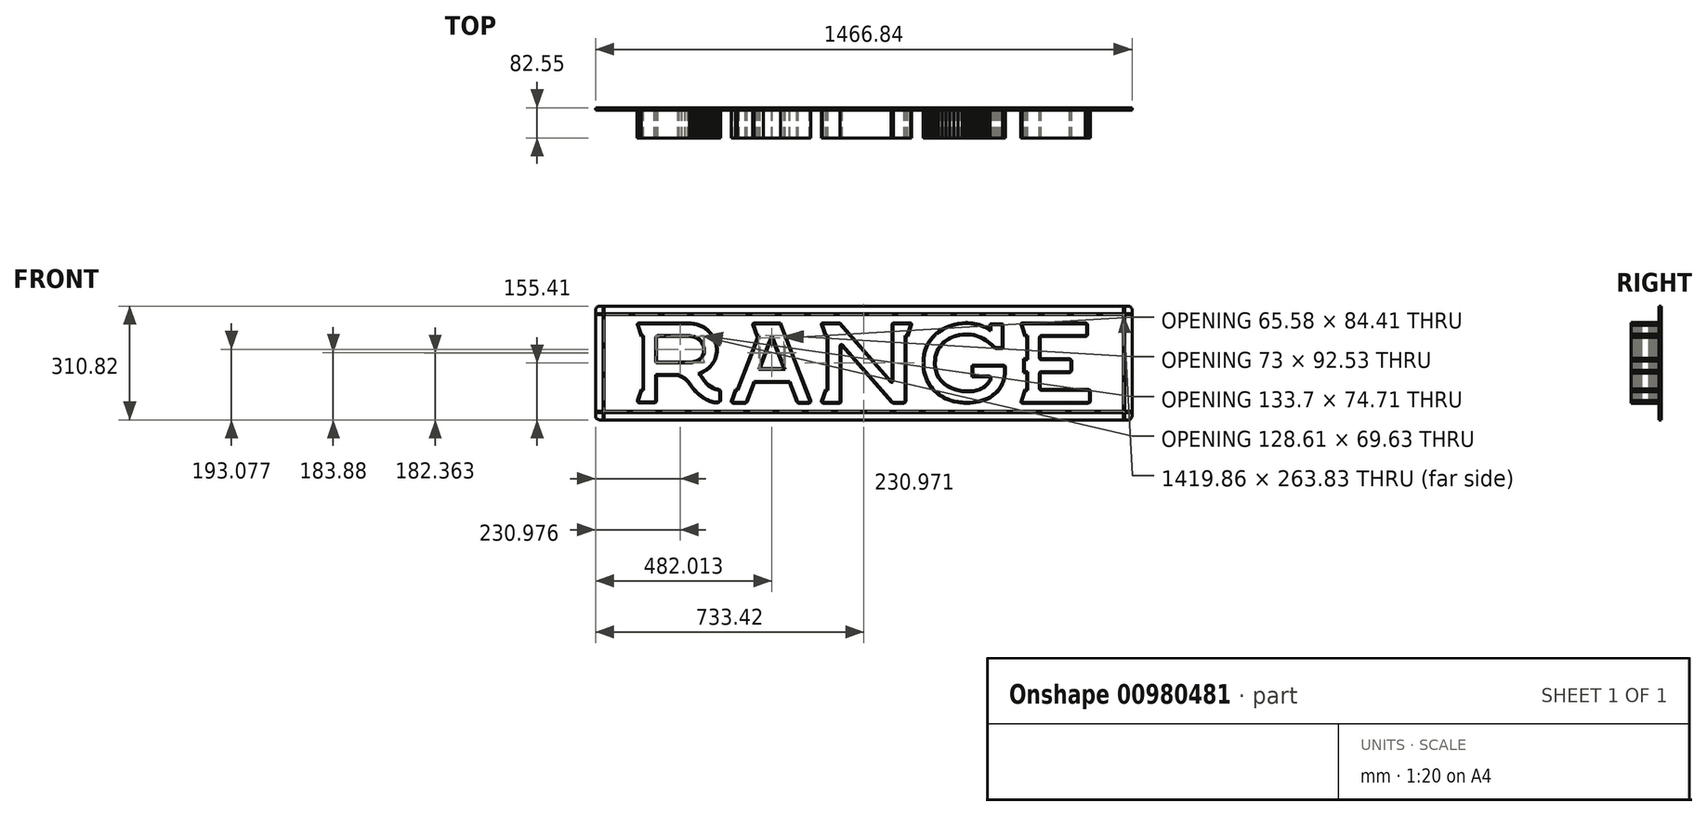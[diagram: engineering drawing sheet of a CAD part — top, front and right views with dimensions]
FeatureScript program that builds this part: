
annotation { "Feature Type Name" : "Feature", "Feature Type Description" : "" }
export const myFeature = defineFeature(function(context is Context, id is Id, definition is map)
    precondition{}
    {
        {
            var Q0;
            Q0=qCreatedBy(makeId("Front.planeOp"),FACE);
            var sketch = newSketch(context, id + "F0", { "sketchPlane" : qUnion([Q0])});
            skLineSegment(sketch, "E0", {"start": v(722.51, -155.4) * mm, "end": v(-722.52, -155.4) * mm});
            skLineSegment(sketch, "E1", {"start": v(-722.52, -155.4) * mm, "end": v(-723.06, -155.4) * mm});
            skLineSegment(sketch, "E2", {"start": v(-723.06, -155.4) * mm, "end": v(-724.71, -155.19) * mm});
            skLineSegment(sketch, "E3", {"start": v(-724.71, -155.19) * mm, "end": v(-726.76, -154.55) * mm});
            skLineSegment(sketch, "E4", {"start": v(-726.76, -154.55) * mm, "end": v(-728.62, -153.55) * mm});
            skLineSegment(sketch, "E5", {"start": v(-728.62, -153.55) * mm, "end": v(-730.23, -152.21) * mm});
            skLineSegment(sketch, "E6", {"start": v(-730.23, -152.21) * mm, "end": v(-731.56, -150.6) * mm});
            skLineSegment(sketch, "E7", {"start": v(-731.56, -150.6) * mm, "end": v(-732.57, -148.75) * mm});
            skLineSegment(sketch, "E8", {"start": v(-732.57, -148.75) * mm, "end": v(-733.2, -146.7) * mm});
            skLineSegment(sketch, "E9", {"start": v(-733.2, -146.7) * mm, "end": v(-733.43, -145.05) * mm});
            skLineSegment(sketch, "E10", {"start": v(-733.43, -145.05) * mm, "end": v(-733.43, -144.5) * mm});
            skLineSegment(sketch, "E11", {"start": v(-733.43, -144.5) * mm, "end": v(-733.43, 144.5) * mm});
            skLineSegment(sketch, "E12", {"start": v(-733.43, 144.5) * mm, "end": v(-733.43, 145.05) * mm});
            skLineSegment(sketch, "E13", {"start": v(-733.43, 145.05) * mm, "end": v(-733.2, 146.7) * mm});
            skLineSegment(sketch, "E14", {"start": v(-733.2, 146.7) * mm, "end": v(-732.57, 148.75) * mm});
            skLineSegment(sketch, "E15", {"start": v(-732.57, 148.75) * mm, "end": v(-731.56, 150.6) * mm});
            skLineSegment(sketch, "E16", {"start": v(-731.56, 150.6) * mm, "end": v(-730.23, 152.21) * mm});
            skLineSegment(sketch, "E17", {"start": v(-730.23, 152.21) * mm, "end": v(-728.62, 153.55) * mm});
            skLineSegment(sketch, "E18", {"start": v(-728.62, 153.55) * mm, "end": v(-726.76, 154.55) * mm});
            skLineSegment(sketch, "E19", {"start": v(-726.76, 154.55) * mm, "end": v(-724.71, 155.19) * mm});
            skLineSegment(sketch, "E20", {"start": v(-724.71, 155.19) * mm, "end": v(-723.06, 155.4) * mm});
            skLineSegment(sketch, "E21", {"start": v(-723.06, 155.4) * mm, "end": v(-722.52, 155.4) * mm});
            skLineSegment(sketch, "E22", {"start": v(-722.52, 155.4) * mm, "end": v(722.51, 155.4) * mm});
            skLineSegment(sketch, "E23", {"start": v(722.51, 155.4) * mm, "end": v(723.06, 155.4) * mm});
            skLineSegment(sketch, "E24", {"start": v(723.06, 155.4) * mm, "end": v(724.71, 155.19) * mm});
            skLineSegment(sketch, "E25", {"start": v(724.71, 155.19) * mm, "end": v(726.76, 154.55) * mm});
            skLineSegment(sketch, "E26", {"start": v(726.76, 154.55) * mm, "end": v(728.61, 153.55) * mm});
            skLineSegment(sketch, "E27", {"start": v(728.61, 153.55) * mm, "end": v(730.23, 152.21) * mm});
            skLineSegment(sketch, "E28", {"start": v(730.23, 152.21) * mm, "end": v(731.56, 150.6) * mm});
            skLineSegment(sketch, "E29", {"start": v(731.56, 150.6) * mm, "end": v(732.57, 148.75) * mm});
            skLineSegment(sketch, "E30", {"start": v(732.57, 148.75) * mm, "end": v(733.2, 146.7) * mm});
            skLineSegment(sketch, "E31", {"start": v(733.2, 146.7) * mm, "end": v(733.43, 145.05) * mm});
            skLineSegment(sketch, "E32", {"start": v(733.43, 145.05) * mm, "end": v(733.43, 144.5) * mm});
            skLineSegment(sketch, "E33", {"start": v(733.43, 144.5) * mm, "end": v(733.43, -144.5) * mm});
            skLineSegment(sketch, "E34", {"start": v(733.43, -144.5) * mm, "end": v(733.43, -145.05) * mm});
            skLineSegment(sketch, "E35", {"start": v(733.43, -145.05) * mm, "end": v(733.2, -146.7) * mm});
            skLineSegment(sketch, "E36", {"start": v(733.2, -146.7) * mm, "end": v(732.57, -148.75) * mm});
            skLineSegment(sketch, "E37", {"start": v(732.57, -148.75) * mm, "end": v(731.56, -150.6) * mm});
            skLineSegment(sketch, "E38", {"start": v(731.56, -150.6) * mm, "end": v(730.23, -152.21) * mm});
            skLineSegment(sketch, "E39", {"start": v(730.23, -152.21) * mm, "end": v(728.61, -153.55) * mm});
            skLineSegment(sketch, "E40", {"start": v(728.61, -153.55) * mm, "end": v(726.76, -154.55) * mm});
            skLineSegment(sketch, "E41", {"start": v(726.76, -154.55) * mm, "end": v(724.71, -155.19) * mm});
            skLineSegment(sketch, "E42", {"start": v(724.71, -155.19) * mm, "end": v(723.06, -155.4) * mm});
            skLineSegment(sketch, "E43", {"start": v(723.06, -155.4) * mm, "end": v(722.51, -155.4) * mm});
            skLineSegment(sketch, "E44", {"start": v(-733.43, 133.51) * mm, "end": v(733.43, 133.51) * mm});
            skLineSegment(sketch, "E45", {"start": v(-733.43, -133.51) * mm, "end": v(733.43, -133.51) * mm});
            skLineSegment(sketch, "E46", {"start": v(-711.53, 155.4) * mm, "end": v(-711.53, -155.4) * mm});
            skLineSegment(sketch, "E47", {"start": v(711.53, 155.4) * mm, "end": v(711.53, -155.4) * mm});
            skLineSegment(sketch, "E48", {"start": v(612.88, -107.15) * mm, "end": v(613.1, -107.15) * mm});
            skLineSegment(sketch, "E49", {"start": v(613.1, -107.15) * mm, "end": v(613.74, -107.06) * mm});
            skLineSegment(sketch, "E50", {"start": v(613.74, -107.06) * mm, "end": v(614.54, -106.82) * mm});
            skLineSegment(sketch, "E51", {"start": v(614.54, -106.82) * mm, "end": v(615.26, -106.42) * mm});
            skLineSegment(sketch, "E52", {"start": v(615.26, -106.42) * mm, "end": v(615.89, -105.9) * mm});
            skLineSegment(sketch, "E53", {"start": v(615.89, -105.9) * mm, "end": v(616.4, -105.27) * mm});
            skLineSegment(sketch, "E54", {"start": v(616.4, -105.27) * mm, "end": v(616.8, -104.55) * mm});
            skLineSegment(sketch, "E55", {"start": v(616.8, -104.55) * mm, "end": v(617.05, -103.75) * mm});
            skLineSegment(sketch, "E56", {"start": v(617.05, -103.75) * mm, "end": v(617.14, -103.1) * mm});
            skLineSegment(sketch, "E57", {"start": v(617.14, -103.1) * mm, "end": v(617.14, -102.9) * mm});
            skLineSegment(sketch, "E58", {"start": v(617.14, -102.9) * mm, "end": v(617.14, -79.01) * mm});
            skLineSegment(sketch, "E59", {"start": v(617.14, -79.01) * mm, "end": v(617.14, -78.8) * mm});
            skLineSegment(sketch, "E60", {"start": v(617.14, -78.8) * mm, "end": v(617.05, -78.15) * mm});
            skLineSegment(sketch, "E61", {"start": v(617.05, -78.15) * mm, "end": v(616.8, -77.35) * mm});
            skLineSegment(sketch, "E62", {"start": v(616.8, -77.35) * mm, "end": v(616.4, -76.63) * mm});
            skLineSegment(sketch, "E63", {"start": v(616.4, -76.63) * mm, "end": v(615.89, -76) * mm});
            skLineSegment(sketch, "E64", {"start": v(615.89, -76) * mm, "end": v(615.26, -75.48) * mm});
            skLineSegment(sketch, "E65", {"start": v(615.26, -75.48) * mm, "end": v(614.54, -75.09) * mm});
            skLineSegment(sketch, "E66", {"start": v(614.54, -75.09) * mm, "end": v(613.74, -74.84) * mm});
            skLineSegment(sketch, "E67", {"start": v(613.74, -74.84) * mm, "end": v(613.1, -74.75) * mm});
            skLineSegment(sketch, "E68", {"start": v(613.1, -74.75) * mm, "end": v(612.88, -74.75) * mm});
            skLineSegment(sketch, "E69", {"start": v(612.88, -74.75) * mm, "end": v(484.52, -74.75) * mm});
            skLineSegment(sketch, "E70", {"start": v(484.52, -74.75) * mm, "end": v(484.3, -74.75) * mm});
            skLineSegment(sketch, "E71", {"start": v(484.3, -74.75) * mm, "end": v(483.65, -74.67) * mm});
            skLineSegment(sketch, "E72", {"start": v(483.65, -74.67) * mm, "end": v(482.85, -74.42) * mm});
            skLineSegment(sketch, "E73", {"start": v(482.85, -74.42) * mm, "end": v(482.12, -74.02) * mm});
            skLineSegment(sketch, "E74", {"start": v(482.12, -74.02) * mm, "end": v(481.48, -73.5) * mm});
            skLineSegment(sketch, "E75", {"start": v(481.48, -73.5) * mm, "end": v(480.96, -72.86) * mm});
            skLineSegment(sketch, "E76", {"start": v(480.96, -72.86) * mm, "end": v(480.57, -72.13) * mm});
            skLineSegment(sketch, "E77", {"start": v(480.57, -72.13) * mm, "end": v(480.31, -71.33) * mm});
            skLineSegment(sketch, "E78", {"start": v(480.31, -71.33) * mm, "end": v(480.23, -70.68) * mm});
            skLineSegment(sketch, "E79", {"start": v(480.23, -70.68) * mm, "end": v(480.23, -70.46) * mm});
            skLineSegment(sketch, "E80", {"start": v(480.23, -70.46) * mm, "end": v(480.23, -27.81) * mm});
            skLineSegment(sketch, "E81", {"start": v(480.23, -27.81) * mm, "end": v(480.23, -27.6) * mm});
            skLineSegment(sketch, "E82", {"start": v(480.23, -27.6) * mm, "end": v(480.31, -26.95) * mm});
            skLineSegment(sketch, "E83", {"start": v(480.31, -26.95) * mm, "end": v(480.57, -26.14) * mm});
            skLineSegment(sketch, "E84", {"start": v(480.57, -26.14) * mm, "end": v(480.96, -25.41) * mm});
            skLineSegment(sketch, "E85", {"start": v(480.96, -25.41) * mm, "end": v(481.48, -24.78) * mm});
            skLineSegment(sketch, "E86", {"start": v(481.48, -24.78) * mm, "end": v(482.12, -24.25) * mm});
            skLineSegment(sketch, "E87", {"start": v(482.12, -24.25) * mm, "end": v(482.85, -23.86) * mm});
            skLineSegment(sketch, "E88", {"start": v(482.85, -23.86) * mm, "end": v(483.65, -23.6) * mm});
            skLineSegment(sketch, "E89", {"start": v(483.65, -23.6) * mm, "end": v(484.3, -23.52) * mm});
            skLineSegment(sketch, "E90", {"start": v(484.3, -23.52) * mm, "end": v(484.52, -23.52) * mm});
            skLineSegment(sketch, "E91", {"start": v(484.52, -23.52) * mm, "end": v(561.84, -23.52) * mm});
            skLineSegment(sketch, "E92", {"start": v(561.84, -23.52) * mm, "end": v(562.05, -23.52) * mm});
            skLineSegment(sketch, "E93", {"start": v(562.05, -23.52) * mm, "end": v(562.7, -23.44) * mm});
            skLineSegment(sketch, "E94", {"start": v(562.7, -23.44) * mm, "end": v(563.5, -23.19) * mm});
            skLineSegment(sketch, "E95", {"start": v(563.5, -23.19) * mm, "end": v(564.22, -22.8) * mm});
            skLineSegment(sketch, "E96", {"start": v(564.22, -22.8) * mm, "end": v(564.85, -22.27) * mm});
            skLineSegment(sketch, "E97", {"start": v(564.85, -22.27) * mm, "end": v(565.37, -21.64) * mm});
            skLineSegment(sketch, "E98", {"start": v(565.37, -21.64) * mm, "end": v(565.76, -20.92) * mm});
            skLineSegment(sketch, "E99", {"start": v(565.76, -20.92) * mm, "end": v(566.01, -20.12) * mm});
            skLineSegment(sketch, "E100", {"start": v(566.01, -20.12) * mm, "end": v(566.1, -19.48) * mm});
            skLineSegment(sketch, "E101", {"start": v(566.1, -19.48) * mm, "end": v(566.1, -19.26) * mm});
            skLineSegment(sketch, "E102", {"start": v(566.1, -19.26) * mm, "end": v(566.1, 4.62) * mm});
            skLineSegment(sketch, "E103", {"start": v(566.1, 4.62) * mm, "end": v(566.1, 4.83) * mm});
            skLineSegment(sketch, "E104", {"start": v(566.1, 4.83) * mm, "end": v(566.01, 5.48) * mm});
            skLineSegment(sketch, "E105", {"start": v(566.01, 5.48) * mm, "end": v(565.76, 6.28) * mm});
            skLineSegment(sketch, "E106", {"start": v(565.76, 6.28) * mm, "end": v(565.37, 7) * mm});
            skLineSegment(sketch, "E107", {"start": v(565.37, 7) * mm, "end": v(564.85, 7.63) * mm});
            skLineSegment(sketch, "E108", {"start": v(564.85, 7.63) * mm, "end": v(564.22, 8.15) * mm});
            skLineSegment(sketch, "E109", {"start": v(564.22, 8.15) * mm, "end": v(563.5, 8.54) * mm});
            skLineSegment(sketch, "E110", {"start": v(563.5, 8.54) * mm, "end": v(562.7, 8.8) * mm});
            skLineSegment(sketch, "E111", {"start": v(562.7, 8.8) * mm, "end": v(562.05, 8.88) * mm});
            skLineSegment(sketch, "E112", {"start": v(562.05, 8.88) * mm, "end": v(561.84, 8.88) * mm});
            skLineSegment(sketch, "E113", {"start": v(561.84, 8.88) * mm, "end": v(484.52, 8.88) * mm});
            skLineSegment(sketch, "E114", {"start": v(484.52, 8.88) * mm, "end": v(484.3, 8.88) * mm});
            skLineSegment(sketch, "E115", {"start": v(484.3, 8.88) * mm, "end": v(483.65, 8.96) * mm});
            skLineSegment(sketch, "E116", {"start": v(483.65, 8.96) * mm, "end": v(482.85, 9.21) * mm});
            skLineSegment(sketch, "E117", {"start": v(482.85, 9.21) * mm, "end": v(482.12, 9.6) * mm});
            skLineSegment(sketch, "E118", {"start": v(482.12, 9.6) * mm, "end": v(481.48, 10.13) * mm});
            skLineSegment(sketch, "E119", {"start": v(481.48, 10.13) * mm, "end": v(480.96, 10.77) * mm});
            skLineSegment(sketch, "E120", {"start": v(480.96, 10.77) * mm, "end": v(480.57, 11.5) * mm});
            skLineSegment(sketch, "E121", {"start": v(480.57, 11.5) * mm, "end": v(480.31, 12.3) * mm});
            skLineSegment(sketch, "E122", {"start": v(480.31, 12.3) * mm, "end": v(480.23, 12.95) * mm});
            skLineSegment(sketch, "E123", {"start": v(480.23, 12.95) * mm, "end": v(480.23, 13.17) * mm});
            skLineSegment(sketch, "E124", {"start": v(480.23, 13.17) * mm, "end": v(480.23, 70.45) * mm});
            skLineSegment(sketch, "E125", {"start": v(480.23, 70.45) * mm, "end": v(480.23, 70.66) * mm});
            skLineSegment(sketch, "E126", {"start": v(480.23, 70.66) * mm, "end": v(480.31, 71.31) * mm});
            skLineSegment(sketch, "E127", {"start": v(480.31, 71.31) * mm, "end": v(480.57, 72.12) * mm});
            skLineSegment(sketch, "E128", {"start": v(480.57, 72.12) * mm, "end": v(480.96, 72.85) * mm});
            skLineSegment(sketch, "E129", {"start": v(480.96, 72.85) * mm, "end": v(481.48, 73.48) * mm});
            skLineSegment(sketch, "E130", {"start": v(481.48, 73.48) * mm, "end": v(482.12, 74) * mm});
            skLineSegment(sketch, "E131", {"start": v(482.12, 74) * mm, "end": v(482.85, 74.4) * mm});
            skLineSegment(sketch, "E132", {"start": v(482.85, 74.4) * mm, "end": v(483.65, 74.65) * mm});
            skLineSegment(sketch, "E133", {"start": v(483.65, 74.65) * mm, "end": v(484.3, 74.74) * mm});
            skLineSegment(sketch, "E134", {"start": v(484.3, 74.74) * mm, "end": v(484.52, 74.74) * mm});
            skLineSegment(sketch, "E135", {"start": v(484.52, 74.74) * mm, "end": v(605.39, 74.74) * mm});
            skLineSegment(sketch, "E136", {"start": v(605.39, 74.74) * mm, "end": v(605.6, 74.74) * mm});
            skLineSegment(sketch, "E137", {"start": v(605.6, 74.74) * mm, "end": v(606.24, 74.82) * mm});
            skLineSegment(sketch, "E138", {"start": v(606.24, 74.82) * mm, "end": v(607.04, 75.07) * mm});
            skLineSegment(sketch, "E139", {"start": v(607.04, 75.07) * mm, "end": v(607.77, 75.46) * mm});
            skLineSegment(sketch, "E140", {"start": v(607.77, 75.46) * mm, "end": v(608.4, 75.98) * mm});
            skLineSegment(sketch, "E141", {"start": v(608.4, 75.98) * mm, "end": v(608.92, 76.61) * mm});
            skLineSegment(sketch, "E142", {"start": v(608.92, 76.61) * mm, "end": v(609.31, 77.34) * mm});
            skLineSegment(sketch, "E143", {"start": v(609.31, 77.34) * mm, "end": v(609.56, 78.14) * mm});
            skLineSegment(sketch, "E144", {"start": v(609.56, 78.14) * mm, "end": v(609.65, 78.78) * mm});
            skLineSegment(sketch, "E145", {"start": v(609.65, 78.78) * mm, "end": v(609.65, 79) * mm});
            skLineSegment(sketch, "E146", {"start": v(609.65, 79) * mm, "end": v(609.65, 102.87) * mm});
            skLineSegment(sketch, "E147", {"start": v(609.65, 102.87) * mm, "end": v(609.65, 103.08) * mm});
            skLineSegment(sketch, "E148", {"start": v(609.65, 103.08) * mm, "end": v(609.56, 103.73) * mm});
            skLineSegment(sketch, "E149", {"start": v(609.56, 103.73) * mm, "end": v(609.31, 104.53) * mm});
            skLineSegment(sketch, "E150", {"start": v(609.31, 104.53) * mm, "end": v(608.92, 105.25) * mm});
            skLineSegment(sketch, "E151", {"start": v(608.92, 105.25) * mm, "end": v(608.4, 105.88) * mm});
            skLineSegment(sketch, "E152", {"start": v(608.4, 105.88) * mm, "end": v(607.77, 106.4) * mm});
            skLineSegment(sketch, "E153", {"start": v(607.77, 106.4) * mm, "end": v(607.04, 106.8) * mm});
            skLineSegment(sketch, "E154", {"start": v(607.04, 106.8) * mm, "end": v(606.24, 107.04) * mm});
            skLineSegment(sketch, "E155", {"start": v(606.24, 107.04) * mm, "end": v(605.6, 107.13) * mm});
            skLineSegment(sketch, "E156", {"start": v(605.6, 107.13) * mm, "end": v(605.39, 107.13) * mm});
            skLineSegment(sketch, "E157", {"start": v(605.39, 107.13) * mm, "end": v(433.74, 107.13) * mm});
            skLineSegment(sketch, "E158", {"start": v(433.74, 107.13) * mm, "end": v(433.54, 107.13) * mm});
            skLineSegment(sketch, "E159", {"start": v(433.54, 107.13) * mm, "end": v(432.94, 106.94) * mm});
            skLineSegment(sketch, "E160", {"start": v(432.94, 106.94) * mm, "end": v(432.4, 106.51) * mm});
            skLineSegment(sketch, "E161", {"start": v(432.4, 106.51) * mm, "end": v(432.31, 106.4) * mm});
            skLineSegment(sketch, "E162", {"start": v(432.31, 106.4) * mm, "end": v(432.23, 106.28) * mm});
            skLineSegment(sketch, "E163", {"start": v(432.23, 106.28) * mm, "end": v(432, 105.64) * mm});
            skLineSegment(sketch, "E164", {"start": v(432, 105.64) * mm, "end": v(432.03, 104.95) * mm});
            skLineSegment(sketch, "E165", {"start": v(432.03, 104.95) * mm, "end": v(432.07, 104.81) * mm});
            skLineSegment(sketch, "E166", {"start": v(432.07, 104.81) * mm, "end": v(442.1, 74.74) * mm});
            skLineSegment(sketch, "E167", {"start": v(442.1, 74.74) * mm, "end": v(447.83, 74.74) * mm});
            skLineSegment(sketch, "E168", {"start": v(447.83, 74.74) * mm, "end": v(447.83, 8.88) * mm});
            skLineSegment(sketch, "E169", {"start": v(447.83, 8.88) * mm, "end": v(438.64, 8.88) * mm});
            skLineSegment(sketch, "E170", {"start": v(438.64, 8.88) * mm, "end": v(438.64, -23.52) * mm});
            skLineSegment(sketch, "E171", {"start": v(438.64, -23.52) * mm, "end": v(447.83, -23.52) * mm});
            skLineSegment(sketch, "E172", {"start": v(447.83, -23.52) * mm, "end": v(447.83, -74.75) * mm});
            skLineSegment(sketch, "E173", {"start": v(447.83, -74.75) * mm, "end": v(442.1, -74.75) * mm});
            skLineSegment(sketch, "E174", {"start": v(442.1, -74.75) * mm, "end": v(432, -105.07) * mm});
            skLineSegment(sketch, "E175", {"start": v(432, -105.07) * mm, "end": v(431.95, -105.19) * mm});
            skLineSegment(sketch, "E176", {"start": v(431.95, -105.19) * mm, "end": v(431.93, -105.8) * mm});
            skLineSegment(sketch, "E177", {"start": v(431.93, -105.8) * mm, "end": v(432.14, -106.39) * mm});
            skLineSegment(sketch, "E178", {"start": v(432.14, -106.39) * mm, "end": v(432.2, -106.5) * mm});
            skLineSegment(sketch, "E179", {"start": v(432.2, -106.5) * mm, "end": v(432.28, -106.6) * mm});
            skLineSegment(sketch, "E180", {"start": v(432.28, -106.6) * mm, "end": v(432.77, -106.98) * mm});
            skLineSegment(sketch, "E181", {"start": v(432.77, -106.98) * mm, "end": v(433.31, -107.15) * mm});
            skLineSegment(sketch, "E182", {"start": v(433.31, -107.15) * mm, "end": v(433.5, -107.15) * mm});
            skLineSegment(sketch, "E183", {"start": v(433.5, -107.15) * mm, "end": v(612.88, -107.15) * mm});
            skLineSegment(sketch, "E184", {"start": v(-569.3, 6.46) * mm, "end": v(-569.3, 68.88) * mm});
            skLineSegment(sketch, "E185", {"start": v(-569.3, 68.88) * mm, "end": v(-569.3, 69.47) * mm});
            skLineSegment(sketch, "E186", {"start": v(-569.3, 69.47) * mm, "end": v(-568.81, 71.27) * mm});
            skLineSegment(sketch, "E187", {"start": v(-568.81, 71.27) * mm, "end": v(-567.49, 73.22) * mm});
            skLineSegment(sketch, "E188", {"start": v(-567.49, 73.22) * mm, "end": v(-565.53, 74.54) * mm});
            skLineSegment(sketch, "E189", {"start": v(-565.53, 74.54) * mm, "end": v(-563.74, 75.02) * mm});
            skLineSegment(sketch, "E190", {"start": v(-563.74, 75.02) * mm, "end": v(-563.14, 75.02) * mm});
            skLineSegment(sketch, "E191", {"start": v(-563.14, 75.02) * mm, "end": v(-477.07, 75.02) * mm});
            skLineSegment(sketch, "E192", {"start": v(-477.07, 75.02) * mm, "end": v(-475.23, 75.02) * mm});
            skLineSegment(sketch, "E193", {"start": v(-475.23, 75.02) * mm, "end": v(-469.7, 74.4) * mm});
            skLineSegment(sketch, "E194", {"start": v(-469.7, 74.4) * mm, "end": v(-462.75, 72.63) * mm});
            skLineSegment(sketch, "E195", {"start": v(-462.75, 72.63) * mm, "end": v(-456.31, 69.79) * mm});
            skLineSegment(sketch, "E196", {"start": v(-456.31, 69.79) * mm, "end": v(-450.52, 65.98) * mm});
            skLineSegment(sketch, "E197", {"start": v(-450.52, 65.98) * mm, "end": v(-445.51, 61.3) * mm});
            skLineSegment(sketch, "E198", {"start": v(-445.51, 61.3) * mm, "end": v(-441.4, 55.84) * mm});
            skLineSegment(sketch, "E199", {"start": v(-441.4, 55.84) * mm, "end": v(-438.3, 49.72) * mm});
            skLineSegment(sketch, "E200", {"start": v(-438.3, 49.72) * mm, "end": v(-436.68, 44.72) * mm});
            skLineSegment(sketch, "E201", {"start": v(-436.68, 44.72) * mm, "end": v(-436.35, 43.02) * mm});
            skLineSegment(sketch, "E202", {"start": v(-436.35, 43.02) * mm, "end": v(-435.97, 41.04) * mm});
            skLineSegment(sketch, "E203", {"start": v(-435.97, 41.04) * mm, "end": v(-435.6, 34.97) * mm});
            skLineSegment(sketch, "E204", {"start": v(-435.6, 34.97) * mm, "end": v(-436.48, 27.4) * mm});
            skLineSegment(sketch, "E205", {"start": v(-436.48, 27.4) * mm, "end": v(-438.97, 20.44) * mm});
            skLineSegment(sketch, "E206", {"start": v(-438.97, 20.44) * mm, "end": v(-441.87, 15.6) * mm});
            skLineSegment(sketch, "E207", {"start": v(-441.87, 15.6) * mm, "end": v(-443.05, 14.17) * mm});
            skLineSegment(sketch, "E208", {"start": v(-443.05, 14.17) * mm, "end": v(-443.73, 13.34) * mm});
            skLineSegment(sketch, "E209", {"start": v(-443.73, 13.34) * mm, "end": v(-446, 11.04) * mm});
            skLineSegment(sketch, "E210", {"start": v(-446, 11.04) * mm, "end": v(-449.32, 8.29) * mm});
            skLineSegment(sketch, "E211", {"start": v(-449.32, 8.29) * mm, "end": v(-453, 5.91) * mm});
            skLineSegment(sketch, "E212", {"start": v(-453, 5.91) * mm, "end": v(-456.99, 3.94) * mm});
            skLineSegment(sketch, "E213", {"start": v(-456.99, 3.94) * mm, "end": v(-461.26, 2.37) * mm});
            skLineSegment(sketch, "E214", {"start": v(-461.26, 2.37) * mm, "end": v(-465.79, 1.24) * mm});
            skLineSegment(sketch, "E215", {"start": v(-465.79, 1.24) * mm, "end": v(-470.52, 0.54) * mm});
            skLineSegment(sketch, "E216", {"start": v(-470.52, 0.54) * mm, "end": v(-474.2, 0.31) * mm});
            skLineSegment(sketch, "E217", {"start": v(-474.2, 0.31) * mm, "end": v(-475.42, 0.31) * mm});
            skLineSegment(sketch, "E218", {"start": v(-475.42, 0.31) * mm, "end": v(-563.14, 0.31) * mm});
            skLineSegment(sketch, "E219", {"start": v(-563.14, 0.31) * mm, "end": v(-563.74, 0.31) * mm});
            skLineSegment(sketch, "E220", {"start": v(-563.74, 0.31) * mm, "end": v(-565.53, 0.8) * mm});
            skLineSegment(sketch, "E221", {"start": v(-565.53, 0.8) * mm, "end": v(-567.49, 2.11) * mm});
            skLineSegment(sketch, "E222", {"start": v(-567.49, 2.11) * mm, "end": v(-568.81, 4.07) * mm});
            skLineSegment(sketch, "E223", {"start": v(-568.81, 4.07) * mm, "end": v(-569.3, 5.86) * mm});
            skLineSegment(sketch, "E224", {"start": v(-569.3, 5.86) * mm, "end": v(-569.3, 6.46) * mm});
            skLineSegment(sketch, "E225", {"start": v(-472.9, -59.01) * mm, "end": v(-471.86, -60.6) * mm});
            skLineSegment(sketch, "E226", {"start": v(-471.86, -60.6) * mm, "end": v(-468.53, -65.25) * mm});
            skLineSegment(sketch, "E227", {"start": v(-468.53, -65.25) * mm, "end": v(-463.99, -71) * mm});
            skLineSegment(sketch, "E228", {"start": v(-463.99, -71) * mm, "end": v(-459.31, -76.26) * mm});
            skLineSegment(sketch, "E229", {"start": v(-459.31, -76.26) * mm, "end": v(-454.54, -81.06) * mm});
            skLineSegment(sketch, "E230", {"start": v(-454.54, -81.06) * mm, "end": v(-449.7, -85.4) * mm});
            skLineSegment(sketch, "E231", {"start": v(-449.7, -85.4) * mm, "end": v(-444.84, -89.3) * mm});
            skLineSegment(sketch, "E232", {"start": v(-444.84, -89.3) * mm, "end": v(-439.99, -92.77) * mm});
            skLineSegment(sketch, "E233", {"start": v(-439.99, -92.77) * mm, "end": v(-435.19, -95.82) * mm});
            skLineSegment(sketch, "E234", {"start": v(-435.19, -95.82) * mm, "end": v(-430.47, -98.47) * mm});
            skLineSegment(sketch, "E235", {"start": v(-430.47, -98.47) * mm, "end": v(-425.87, -100.73) * mm});
            skLineSegment(sketch, "E236", {"start": v(-425.87, -100.73) * mm, "end": v(-421.43, -102.62) * mm});
            skLineSegment(sketch, "E237", {"start": v(-421.43, -102.62) * mm, "end": v(-417.18, -104.14) * mm});
            skLineSegment(sketch, "E238", {"start": v(-417.18, -104.14) * mm, "end": v(-413.16, -105.31) * mm});
            skLineSegment(sketch, "E239", {"start": v(-413.16, -105.31) * mm, "end": v(-409.4, -106.15) * mm});
            skLineSegment(sketch, "E240", {"start": v(-409.4, -106.15) * mm, "end": v(-405.95, -106.66) * mm});
            skLineSegment(sketch, "E241", {"start": v(-405.95, -106.66) * mm, "end": v(-403.61, -106.85) * mm});
            skLineSegment(sketch, "E242", {"start": v(-403.61, -106.85) * mm, "end": v(-402.84, -106.86) * mm});
            skLineSegment(sketch, "E243", {"start": v(-402.84, -106.86) * mm, "end": v(-402.13, -106.86) * mm});
            skLineSegment(sketch, "E244", {"start": v(-402.13, -106.86) * mm, "end": v(-398.9, -106.23) * mm});
            skLineSegment(sketch, "E245", {"start": v(-398.9, -106.23) * mm, "end": v(-396.26, -104.76) * mm});
            skLineSegment(sketch, "E246", {"start": v(-396.26, -104.76) * mm, "end": v(-395.84, -104.36) * mm});
            skLineSegment(sketch, "E247", {"start": v(-395.84, -104.36) * mm, "end": v(-395.6, -104.12) * mm});
            skLineSegment(sketch, "E248", {"start": v(-395.6, -104.12) * mm, "end": v(-394.97, -103.3) * mm});
            skLineSegment(sketch, "E249", {"start": v(-394.97, -103.3) * mm, "end": v(-394.34, -102.12) * mm});
            skLineSegment(sketch, "E250", {"start": v(-394.34, -102.12) * mm, "end": v(-393.95, -100.82) * mm});
            skLineSegment(sketch, "E251", {"start": v(-393.95, -100.82) * mm, "end": v(-393.82, -99.77) * mm});
            skLineSegment(sketch, "E252", {"start": v(-393.82, -99.77) * mm, "end": v(-393.82, -99.42) * mm});
            skLineSegment(sketch, "E253", {"start": v(-393.82, -99.42) * mm, "end": v(-393.85, -80.15) * mm});
            skLineSegment(sketch, "E254", {"start": v(-393.85, -80.15) * mm, "end": v(-393.85, -79.63) * mm});
            skLineSegment(sketch, "E255", {"start": v(-393.85, -79.63) * mm, "end": v(-394.21, -78.07) * mm});
            skLineSegment(sketch, "E256", {"start": v(-394.21, -78.07) * mm, "end": v(-395.21, -76.3) * mm});
            skLineSegment(sketch, "E257", {"start": v(-395.21, -76.3) * mm, "end": v(-396.73, -74.96) * mm});
            skLineSegment(sketch, "E258", {"start": v(-396.73, -74.96) * mm, "end": v(-398.16, -74.3) * mm});
            skLineSegment(sketch, "E259", {"start": v(-398.16, -74.3) * mm, "end": v(-398.65, -74.2) * mm});
            skLineSegment(sketch, "E260", {"start": v(-398.65, -74.2) * mm, "end": v(-399.75, -73.99) * mm});
            skLineSegment(sketch, "E261", {"start": v(-399.75, -73.99) * mm, "end": v(-403.01, -73.18) * mm});
            skLineSegment(sketch, "E262", {"start": v(-403.01, -73.18) * mm, "end": v(-408.05, -71.55) * mm});
            skLineSegment(sketch, "E263", {"start": v(-408.05, -71.55) * mm, "end": v(-413.6, -69.2) * mm});
            skLineSegment(sketch, "E264", {"start": v(-413.6, -69.2) * mm, "end": v(-419.45, -65.98) * mm});
            skLineSegment(sketch, "E265", {"start": v(-419.45, -65.98) * mm, "end": v(-425.46, -61.77) * mm});
            skLineSegment(sketch, "E266", {"start": v(-425.46, -61.77) * mm, "end": v(-431.42, -56.42) * mm});
            skLineSegment(sketch, "E267", {"start": v(-431.42, -56.42) * mm, "end": v(-437.17, -49.8) * mm});
            skLineSegment(sketch, "E268", {"start": v(-437.17, -49.8) * mm, "end": v(-441.31, -43.86) * mm});
            skLineSegment(sketch, "E269", {"start": v(-441.31, -43.86) * mm, "end": v(-442.52, -41.78) * mm});
            skLineSegment(sketch, "E270", {"start": v(-442.52, -41.78) * mm, "end": v(-443.1, -40.78) * mm});
            skLineSegment(sketch, "E271", {"start": v(-443.1, -40.78) * mm, "end": v(-446.55, -35.78) * mm});
            skLineSegment(sketch, "E272", {"start": v(-446.55, -35.78) * mm, "end": v(-450.7, -30.84) * mm});
            skLineSegment(sketch, "E273", {"start": v(-450.7, -30.84) * mm, "end": v(-451.62, -29.86) * mm});
            skLineSegment(sketch, "E274", {"start": v(-451.62, -29.86) * mm, "end": v(-452.97, -28.45) * mm});
            skLineSegment(sketch, "E275", {"start": v(-452.97, -28.45) * mm, "end": v(-451.12, -27.8) * mm});
            skLineSegment(sketch, "E276", {"start": v(-451.12, -27.8) * mm, "end": v(-449.62, -27.27) * mm});
            skLineSegment(sketch, "E277", {"start": v(-449.62, -27.27) * mm, "end": v(-445.2, -25.47) * mm});
            skLineSegment(sketch, "E278", {"start": v(-445.2, -25.47) * mm, "end": v(-439.6, -22.8) * mm});
            skLineSegment(sketch, "E279", {"start": v(-439.6, -22.8) * mm, "end": v(-434.38, -19.78) * mm});
            skLineSegment(sketch, "E280", {"start": v(-434.38, -19.78) * mm, "end": v(-429.52, -16.45) * mm});
            skLineSegment(sketch, "E281", {"start": v(-429.52, -16.45) * mm, "end": v(-425.03, -12.82) * mm});
            skLineSegment(sketch, "E282", {"start": v(-425.03, -12.82) * mm, "end": v(-420.93, -8.9) * mm});
            skLineSegment(sketch, "E283", {"start": v(-420.93, -8.9) * mm, "end": v(-417.24, -4.7) * mm});
            skLineSegment(sketch, "E284", {"start": v(-417.24, -4.7) * mm, "end": v(-413.95, -0.26) * mm});
            skLineSegment(sketch, "E285", {"start": v(-413.95, -0.26) * mm, "end": v(-411.07, 4.43) * mm});
            skLineSegment(sketch, "E286", {"start": v(-411.07, 4.43) * mm, "end": v(-408.63, 9.34) * mm});
            skLineSegment(sketch, "E287", {"start": v(-408.63, 9.34) * mm, "end": v(-406.63, 14.46) * mm});
            skLineSegment(sketch, "E288", {"start": v(-406.63, 14.46) * mm, "end": v(-405.08, 19.78) * mm});
            skLineSegment(sketch, "E289", {"start": v(-405.08, 19.78) * mm, "end": v(-403.99, 25.27) * mm});
            skLineSegment(sketch, "E290", {"start": v(-403.99, 25.27) * mm, "end": v(-403.37, 30.93) * mm});
            skLineSegment(sketch, "E291", {"start": v(-403.37, 30.93) * mm, "end": v(-403.23, 36.74) * mm});
            skLineSegment(sketch, "E292", {"start": v(-403.23, 36.74) * mm, "end": v(-403.44, 41.2) * mm});
            skLineSegment(sketch, "E293", {"start": v(-403.44, 41.2) * mm, "end": v(-403.59, 42.67) * mm});
            skLineSegment(sketch, "E294", {"start": v(-403.59, 42.67) * mm, "end": v(-403.75, 44.36) * mm});
            skLineSegment(sketch, "E295", {"start": v(-403.75, 44.36) * mm, "end": v(-404.6, 49.39) * mm});
            skLineSegment(sketch, "E296", {"start": v(-404.6, 49.39) * mm, "end": v(-406.28, 55.88) * mm});
            skLineSegment(sketch, "E297", {"start": v(-406.28, 55.88) * mm, "end": v(-408.57, 62.13) * mm});
            skLineSegment(sketch, "E298", {"start": v(-408.57, 62.13) * mm, "end": v(-411.45, 68.1) * mm});
            skLineSegment(sketch, "E299", {"start": v(-411.45, 68.1) * mm, "end": v(-414.87, 73.78) * mm});
            skLineSegment(sketch, "E300", {"start": v(-414.87, 73.78) * mm, "end": v(-418.8, 79.12) * mm});
            skLineSegment(sketch, "E301", {"start": v(-418.8, 79.12) * mm, "end": v(-423.22, 84.09) * mm});
            skLineSegment(sketch, "E302", {"start": v(-423.22, 84.09) * mm, "end": v(-428.07, 88.66) * mm});
            skLineSegment(sketch, "E303", {"start": v(-428.07, 88.66) * mm, "end": v(-433.34, 92.81) * mm});
            skLineSegment(sketch, "E304", {"start": v(-433.34, 92.81) * mm, "end": v(-438.97, 96.5) * mm});
            skLineSegment(sketch, "E305", {"start": v(-438.97, 96.5) * mm, "end": v(-444.95, 99.72) * mm});
            skLineSegment(sketch, "E306", {"start": v(-444.95, 99.72) * mm, "end": v(-451.23, 102.41) * mm});
            skLineSegment(sketch, "E307", {"start": v(-451.23, 102.41) * mm, "end": v(-457.77, 104.56) * mm});
            skLineSegment(sketch, "E308", {"start": v(-457.77, 104.56) * mm, "end": v(-464.55, 106.13) * mm});
            skLineSegment(sketch, "E309", {"start": v(-464.55, 106.13) * mm, "end": v(-471.53, 107.1) * mm});
            skLineSegment(sketch, "E310", {"start": v(-471.53, 107.1) * mm, "end": v(-476.88, 107.42) * mm});
            skLineSegment(sketch, "E311", {"start": v(-476.88, 107.42) * mm, "end": v(-478.66, 107.42) * mm});
            skLineSegment(sketch, "E312", {"start": v(-478.66, 107.42) * mm, "end": v(-608, 107.42) * mm});
            skLineSegment(sketch, "E313", {"start": v(-608, 107.42) * mm, "end": v(-609.1, 107.42) * mm});
            skLineSegment(sketch, "E314", {"start": v(-609.1, 107.42) * mm, "end": v(-612.45, 107.22) * mm});
            skLineSegment(sketch, "E315", {"start": v(-612.45, 107.22) * mm, "end": v(-615.16, 106.76) * mm});
            skLineSegment(sketch, "E316", {"start": v(-615.16, 106.76) * mm, "end": v(-616.54, 106.22) * mm});
            skLineSegment(sketch, "E317", {"start": v(-616.54, 106.22) * mm, "end": v(-616.97, 105.9) * mm});
            skLineSegment(sketch, "E318", {"start": v(-616.97, 105.9) * mm, "end": v(-617.04, 105.81) * mm});
            skLineSegment(sketch, "E319", {"start": v(-617.04, 105.81) * mm, "end": v(-617.05, 105.79) * mm});
            skLineSegment(sketch, "E320", {"start": v(-617.05, 105.79) * mm, "end": v(-617.13, 105.6) * mm});
            skLineSegment(sketch, "E321", {"start": v(-617.13, 105.6) * mm, "end": v(-617.1, 105.23) * mm});
            skLineSegment(sketch, "E322", {"start": v(-617.1, 105.23) * mm, "end": v(-617.06, 105.13) * mm});
            skLineSegment(sketch, "E323", {"start": v(-617.06, 105.13) * mm, "end": v(-607.03, 75.02) * mm});
            skLineSegment(sketch, "E324", {"start": v(-607.03, 75.02) * mm, "end": v(-601.69, 75.02) * mm});
            skLineSegment(sketch, "E325", {"start": v(-601.69, 75.02) * mm, "end": v(-601.69, -74.47) * mm});
            skLineSegment(sketch, "E326", {"start": v(-601.69, -74.47) * mm, "end": v(-607.03, -74.47) * mm});
            skLineSegment(sketch, "E327", {"start": v(-607.03, -74.47) * mm, "end": v(-616.48, -102.81) * mm});
            skLineSegment(sketch, "E328", {"start": v(-616.48, -102.81) * mm, "end": v(-616.56, -103.05) * mm});
            skLineSegment(sketch, "E329", {"start": v(-616.56, -103.05) * mm, "end": v(-616.6, -104.25) * mm});
            skLineSegment(sketch, "E330", {"start": v(-616.6, -104.25) * mm, "end": v(-616.2, -105.38) * mm});
            skLineSegment(sketch, "E331", {"start": v(-616.2, -105.38) * mm, "end": v(-616.06, -105.59) * mm});
            skLineSegment(sketch, "E332", {"start": v(-616.06, -105.59) * mm, "end": v(-615.91, -105.79) * mm});
            skLineSegment(sketch, "E333", {"start": v(-615.91, -105.79) * mm, "end": v(-614.96, -106.53) * mm});
            skLineSegment(sketch, "E334", {"start": v(-614.96, -106.53) * mm, "end": v(-613.9, -106.87) * mm});
            skLineSegment(sketch, "E335", {"start": v(-613.9, -106.87) * mm, "end": v(-613.56, -106.87) * mm});
            skLineSegment(sketch, "E336", {"start": v(-613.56, -106.87) * mm, "end": v(-573.44, -106.86) * mm});
            skLineSegment(sketch, "E337", {"start": v(-573.44, -106.86) * mm, "end": v(-573.04, -106.86) * mm});
            skLineSegment(sketch, "E338", {"start": v(-573.04, -106.86) * mm, "end": v(-571.82, -106.53) * mm});
            skLineSegment(sketch, "E339", {"start": v(-571.82, -106.53) * mm, "end": v(-570.5, -105.64) * mm});
            skLineSegment(sketch, "E340", {"start": v(-570.5, -105.64) * mm, "end": v(-569.6, -104.31) * mm});
            skLineSegment(sketch, "E341", {"start": v(-569.6, -104.31) * mm, "end": v(-569.27, -103.1) * mm});
            skLineSegment(sketch, "E342", {"start": v(-569.27, -103.1) * mm, "end": v(-569.27, -102.69) * mm});
            skLineSegment(sketch, "E343", {"start": v(-569.27, -102.69) * mm, "end": v(-569.3, -34.03) * mm});
            skLineSegment(sketch, "E344", {"start": v(-569.3, -34.03) * mm, "end": v(-569.3, -33.84) * mm});
            skLineSegment(sketch, "E345", {"start": v(-569.3, -33.84) * mm, "end": v(-569.14, -33.27) * mm});
            skLineSegment(sketch, "E346", {"start": v(-569.14, -33.27) * mm, "end": v(-568.72, -32.65) * mm});
            skLineSegment(sketch, "E347", {"start": v(-568.72, -32.65) * mm, "end": v(-568.1, -32.24) * mm});
            skLineSegment(sketch, "E348", {"start": v(-568.1, -32.24) * mm, "end": v(-567.54, -32.08) * mm});
            skLineSegment(sketch, "E349", {"start": v(-567.54, -32.08) * mm, "end": v(-567.35, -32.08) * mm});
            skLineSegment(sketch, "E350", {"start": v(-567.35, -32.08) * mm, "end": v(-507.42, -32.05) * mm});
            skLineSegment(sketch, "E351", {"start": v(-507.42, -32.05) * mm, "end": v(-504.81, -32.9) * mm});
            skLineSegment(sketch, "E352", {"start": v(-504.81, -32.9) * mm, "end": v(-497.27, -36.37) * mm});
            skLineSegment(sketch, "E353", {"start": v(-497.27, -36.37) * mm, "end": v(-488.12, -42.32) * mm});
            skLineSegment(sketch, "E354", {"start": v(-488.12, -42.32) * mm, "end": v(-479.99, -49.87) * mm});
            skLineSegment(sketch, "E355", {"start": v(-479.99, -49.87) * mm, "end": v(-474.5, -56.6) * mm});
            skLineSegment(sketch, "E356", {"start": v(-474.5, -56.6) * mm, "end": v(-472.9, -59.01) * mm});
            skLineSegment(sketch, "E357", {"start": v(161.63, -0.34) * mm, "end": v(161.63, -2.42) * mm});
            skLineSegment(sketch, "E358", {"start": v(161.63, -2.42) * mm, "end": v(161.9, -8.67) * mm});
            skLineSegment(sketch, "E359", {"start": v(161.9, -8.67) * mm, "end": v(162.71, -16.77) * mm});
            skLineSegment(sketch, "E360", {"start": v(162.71, -16.77) * mm, "end": v(164.06, -24.64) * mm});
            skLineSegment(sketch, "E361", {"start": v(164.06, -24.64) * mm, "end": v(165.92, -32.26) * mm});
            skLineSegment(sketch, "E362", {"start": v(165.92, -32.26) * mm, "end": v(168.29, -39.62) * mm});
            skLineSegment(sketch, "E363", {"start": v(168.29, -39.62) * mm, "end": v(171.16, -46.7) * mm});
            skLineSegment(sketch, "E364", {"start": v(171.16, -46.7) * mm, "end": v(174.52, -53.5) * mm});
            skLineSegment(sketch, "E365", {"start": v(174.52, -53.5) * mm, "end": v(178.37, -59.99) * mm});
            skLineSegment(sketch, "E366", {"start": v(178.37, -59.99) * mm, "end": v(182.7, -66.17) * mm});
            skLineSegment(sketch, "E367", {"start": v(182.7, -66.17) * mm, "end": v(187.49, -72.01) * mm});
            skLineSegment(sketch, "E368", {"start": v(187.49, -72.01) * mm, "end": v(192.74, -77.51) * mm});
            skLineSegment(sketch, "E369", {"start": v(192.74, -77.51) * mm, "end": v(198.43, -82.66) * mm});
            skLineSegment(sketch, "E370", {"start": v(198.43, -82.66) * mm, "end": v(204.57, -87.44) * mm});
            skLineSegment(sketch, "E371", {"start": v(204.57, -87.44) * mm, "end": v(211.15, -91.83) * mm});
            skLineSegment(sketch, "E372", {"start": v(211.15, -91.83) * mm, "end": v(218.14, -95.82) * mm});
            skLineSegment(sketch, "E373", {"start": v(218.14, -95.82) * mm, "end": v(223.66, -98.57) * mm});
            skLineSegment(sketch, "E374", {"start": v(223.66, -98.57) * mm, "end": v(225.54, -99.4) * mm});
            skLineSegment(sketch, "E375", {"start": v(225.54, -99.4) * mm, "end": v(228.05, -100.51) * mm});
            skLineSegment(sketch, "E376", {"start": v(228.05, -100.51) * mm, "end": v(235.83, -103.2) * mm});
            skLineSegment(sketch, "E377", {"start": v(235.83, -103.2) * mm, "end": v(246.43, -105.95) * mm});
            skLineSegment(sketch, "E378", {"start": v(246.43, -105.95) * mm, "end": v(256.81, -107.87) * mm});
            skLineSegment(sketch, "E379", {"start": v(256.81, -107.87) * mm, "end": v(264.02, -108.9) * mm});
            skLineSegment(sketch, "E380", {"start": v(264.02, -108.9) * mm, "end": v(266.43, -109.2) * mm});
            skLineSegment(sketch, "E381", {"start": v(266.43, -109.2) * mm, "end": v(268.4, -109.43) * mm});
            skLineSegment(sketch, "E382", {"start": v(268.4, -109.43) * mm, "end": v(274.36, -109.92) * mm});
            skLineSegment(sketch, "E383", {"start": v(274.36, -109.92) * mm, "end": v(282.45, -110.2) * mm});
            skLineSegment(sketch, "E384", {"start": v(282.45, -110.2) * mm, "end": v(290.63, -110.01) * mm});
            skLineSegment(sketch, "E385", {"start": v(290.63, -110.01) * mm, "end": v(298.85, -109.35) * mm});
            skLineSegment(sketch, "E386", {"start": v(298.85, -109.35) * mm, "end": v(307.06, -108.18) * mm});
            skLineSegment(sketch, "E387", {"start": v(307.06, -108.18) * mm, "end": v(315.19, -106.51) * mm});
            skLineSegment(sketch, "E388", {"start": v(315.19, -106.51) * mm, "end": v(323.17, -104.32) * mm});
            skLineSegment(sketch, "E389", {"start": v(323.17, -104.32) * mm, "end": v(330.96, -101.58) * mm});
            skLineSegment(sketch, "E390", {"start": v(330.96, -101.58) * mm, "end": v(338.5, -98.3) * mm});
            skLineSegment(sketch, "E391", {"start": v(338.5, -98.3) * mm, "end": v(345.7, -94.45) * mm});
            skLineSegment(sketch, "E392", {"start": v(345.7, -94.45) * mm, "end": v(352.55, -90.03) * mm});
            skLineSegment(sketch, "E393", {"start": v(352.55, -90.03) * mm, "end": v(358.96, -85.01) * mm});
            skLineSegment(sketch, "E394", {"start": v(358.96, -85.01) * mm, "end": v(364.87, -79.38) * mm});
            skLineSegment(sketch, "E395", {"start": v(364.87, -79.38) * mm, "end": v(370.22, -73.14) * mm});
            skLineSegment(sketch, "E396", {"start": v(370.22, -73.14) * mm, "end": v(374.97, -66.26) * mm});
            skLineSegment(sketch, "E397", {"start": v(374.97, -66.26) * mm, "end": v(378.13, -60.66) * mm});
            skLineSegment(sketch, "E398", {"start": v(378.13, -60.66) * mm, "end": v(379.05, -58.73) * mm});
            skLineSegment(sketch, "E399", {"start": v(379.05, -58.73) * mm, "end": v(379.7, -57.33) * mm});
            skLineSegment(sketch, "E400", {"start": v(379.7, -57.33) * mm, "end": v(381.48, -53.01) * mm});
            skLineSegment(sketch, "E401", {"start": v(381.48, -53.01) * mm, "end": v(383.49, -47.05) * mm});
            skLineSegment(sketch, "E402", {"start": v(383.49, -47.05) * mm, "end": v(385.07, -40.86) * mm});
            skLineSegment(sketch, "E403", {"start": v(385.07, -40.86) * mm, "end": v(385.98, -36.07) * mm});
            skLineSegment(sketch, "E404", {"start": v(385.98, -36.07) * mm, "end": v(386.21, -34.46) * mm});
            skLineSegment(sketch, "E405", {"start": v(386.21, -34.46) * mm, "end": v(386.42, -32.98) * mm});
            skLineSegment(sketch, "E406", {"start": v(386.42, -32.98) * mm, "end": v(386.85, -28.53) * mm});
            skLineSegment(sketch, "E407", {"start": v(386.85, -28.53) * mm, "end": v(387.15, -22.57) * mm});
            skLineSegment(sketch, "E408", {"start": v(387.15, -22.57) * mm, "end": v(387.24, -16.72) * mm});
            skLineSegment(sketch, "E409", {"start": v(387.24, -16.72) * mm, "end": v(387.23, -12.51) * mm});
            skLineSegment(sketch, "E410", {"start": v(387.23, -12.51) * mm, "end": v(387.22, -11.1) * mm});
            skLineSegment(sketch, "E411", {"start": v(387.22, -11.1) * mm, "end": v(387.22, -10.89) * mm});
            skLineSegment(sketch, "E412", {"start": v(387.22, -10.89) * mm, "end": v(387.12, -10.23) * mm});
            skLineSegment(sketch, "E413", {"start": v(387.12, -10.23) * mm, "end": v(386.86, -9.4) * mm});
            skLineSegment(sketch, "E414", {"start": v(386.86, -9.4) * mm, "end": v(386.44, -8.66) * mm});
            skLineSegment(sketch, "E415", {"start": v(386.44, -8.66) * mm, "end": v(385.89, -8.02) * mm});
            skLineSegment(sketch, "E416", {"start": v(385.89, -8.02) * mm, "end": v(385.22, -7.48) * mm});
            skLineSegment(sketch, "E417", {"start": v(385.22, -7.48) * mm, "end": v(384.46, -7.08) * mm});
            skLineSegment(sketch, "E418", {"start": v(384.46, -7.08) * mm, "end": v(383.61, -6.82) * mm});
            skLineSegment(sketch, "E419", {"start": v(383.61, -6.82) * mm, "end": v(382.94, -6.74) * mm});
            skLineSegment(sketch, "E420", {"start": v(382.94, -6.74) * mm, "end": v(382.71, -6.74) * mm});
            skLineSegment(sketch, "E421", {"start": v(382.71, -6.74) * mm, "end": v(297.4, -6.74) * mm});
            skLineSegment(sketch, "E422", {"start": v(297.4, -6.74) * mm, "end": v(297.26, -6.74) * mm});
            skLineSegment(sketch, "E423", {"start": v(297.26, -6.74) * mm, "end": v(296.88, -6.84) * mm});
            skLineSegment(sketch, "E424", {"start": v(296.88, -6.84) * mm, "end": v(296.46, -7.11) * mm});
            skLineSegment(sketch, "E425", {"start": v(296.46, -7.11) * mm, "end": v(296.17, -7.53) * mm});
            skLineSegment(sketch, "E426", {"start": v(296.17, -7.53) * mm, "end": v(296.07, -7.9) * mm});
            skLineSegment(sketch, "E427", {"start": v(296.07, -7.9) * mm, "end": v(296.07, -8.03) * mm});
            skLineSegment(sketch, "E428", {"start": v(296.07, -8.03) * mm, "end": v(296.07, -36.86) * mm});
            skLineSegment(sketch, "E429", {"start": v(296.07, -36.86) * mm, "end": v(296.07, -36.98) * mm});
            skLineSegment(sketch, "E430", {"start": v(296.07, -36.98) * mm, "end": v(296.17, -37.36) * mm});
            skLineSegment(sketch, "E431", {"start": v(296.17, -37.36) * mm, "end": v(296.46, -37.77) * mm});
            skLineSegment(sketch, "E432", {"start": v(296.46, -37.77) * mm, "end": v(296.88, -38.05) * mm});
            skLineSegment(sketch, "E433", {"start": v(296.88, -38.05) * mm, "end": v(297.26, -38.15) * mm});
            skLineSegment(sketch, "E434", {"start": v(297.26, -38.15) * mm, "end": v(297.4, -38.15) * mm});
            skLineSegment(sketch, "E435", {"start": v(297.4, -38.15) * mm, "end": v(341.82, -38.15) * mm});
            skLineSegment(sketch, "E436", {"start": v(341.82, -38.15) * mm, "end": v(342.16, -38.15) * mm});
            skLineSegment(sketch, "E437", {"start": v(342.16, -38.15) * mm, "end": v(343.16, -38.32) * mm});
            skLineSegment(sketch, "E438", {"start": v(343.16, -38.32) * mm, "end": v(344.12, -38.74) * mm});
            skLineSegment(sketch, "E439", {"start": v(344.12, -38.74) * mm, "end": v(344.76, -39.32) * mm});
            skLineSegment(sketch, "E440", {"start": v(344.76, -39.32) * mm, "end": v(345.07, -39.79) * mm});
            skLineSegment(sketch, "E441", {"start": v(345.07, -39.79) * mm, "end": v(345.14, -39.95) * mm});
            skLineSegment(sketch, "E442", {"start": v(345.14, -39.95) * mm, "end": v(345.34, -40.4) * mm});
            skLineSegment(sketch, "E443", {"start": v(345.34, -40.4) * mm, "end": v(345.4, -41.95) * mm});
            skLineSegment(sketch, "E444", {"start": v(345.4, -41.95) * mm, "end": v(344.8, -44.4) * mm});
            skLineSegment(sketch, "E445", {"start": v(344.8, -44.4) * mm, "end": v(343.6, -47.06) * mm});
            skLineSegment(sketch, "E446", {"start": v(343.6, -47.06) * mm, "end": v(342.04, -49.74) * mm});
            skLineSegment(sketch, "E447", {"start": v(342.04, -49.74) * mm, "end": v(340.37, -52.2) * mm});
            skLineSegment(sketch, "E448", {"start": v(340.37, -52.2) * mm, "end": v(338.86, -54.25) * mm});
            skLineSegment(sketch, "E449", {"start": v(338.86, -54.25) * mm, "end": v(337.75, -55.65) * mm});
            skLineSegment(sketch, "E450", {"start": v(337.75, -55.65) * mm, "end": v(337.33, -56.17) * mm});
            skLineSegment(sketch, "E451", {"start": v(337.33, -56.17) * mm, "end": v(337.3, -56.2) * mm});
            skLineSegment(sketch, "E452", {"start": v(337.3, -56.2) * mm, "end": v(336.28, -57.37) * mm});
            skLineSegment(sketch, "E453", {"start": v(336.28, -57.37) * mm, "end": v(332.9, -60.66) * mm});
            skLineSegment(sketch, "E454", {"start": v(332.9, -60.66) * mm, "end": v(327.93, -64.62) * mm});
            skLineSegment(sketch, "E455", {"start": v(327.93, -64.62) * mm, "end": v(322.46, -68.02) * mm});
            skLineSegment(sketch, "E456", {"start": v(322.46, -68.02) * mm, "end": v(318.06, -70.21) * mm});
            skLineSegment(sketch, "E457", {"start": v(318.06, -70.21) * mm, "end": v(316.55, -70.83) * mm});
            skLineSegment(sketch, "E458", {"start": v(316.55, -70.83) * mm, "end": v(314.53, -71.65) * mm});
            skLineSegment(sketch, "E459", {"start": v(314.53, -71.65) * mm, "end": v(308.22, -73.58) * mm});
            skLineSegment(sketch, "E460", {"start": v(308.22, -73.58) * mm, "end": v(299.12, -75.4) * mm});
            skLineSegment(sketch, "E461", {"start": v(299.12, -75.4) * mm, "end": v(289.48, -76.3) * mm});
            skLineSegment(sketch, "E462", {"start": v(289.48, -76.3) * mm, "end": v(279.48, -76.3) * mm});
            skLineSegment(sketch, "E463", {"start": v(279.48, -76.3) * mm, "end": v(269.35, -75.4) * mm});
            skLineSegment(sketch, "E464", {"start": v(269.35, -75.4) * mm, "end": v(259.3, -73.6) * mm});
            skLineSegment(sketch, "E465", {"start": v(259.3, -73.6) * mm, "end": v(249.52, -70.93) * mm});
            skLineSegment(sketch, "E466", {"start": v(249.52, -70.93) * mm, "end": v(242.5, -68.39) * mm});
            skLineSegment(sketch, "E467", {"start": v(242.5, -68.39) * mm, "end": v(240.23, -67.38) * mm});
            skLineSegment(sketch, "E468", {"start": v(240.23, -67.38) * mm, "end": v(237.55, -66.2) * mm});
            skLineSegment(sketch, "E469", {"start": v(237.55, -66.2) * mm, "end": v(229.8, -62.02) * mm});
            skLineSegment(sketch, "E470", {"start": v(229.8, -62.02) * mm, "end": v(220.76, -55.78) * mm});
            skLineSegment(sketch, "E471", {"start": v(220.76, -55.78) * mm, "end": v(213.1, -48.67) * mm});
            skLineSegment(sketch, "E472", {"start": v(213.1, -48.67) * mm, "end": v(206.8, -40.7) * mm});
            skLineSegment(sketch, "E473", {"start": v(206.8, -40.7) * mm, "end": v(201.91, -31.86) * mm});
            skLineSegment(sketch, "E474", {"start": v(201.91, -31.86) * mm, "end": v(198.4, -22.18) * mm});
            skLineSegment(sketch, "E475", {"start": v(198.4, -22.18) * mm, "end": v(196.3, -11.66) * mm});
            skLineSegment(sketch, "E476", {"start": v(196.3, -11.66) * mm, "end": v(195.6, -3.14) * mm});
            skLineSegment(sketch, "E477", {"start": v(195.6, -3.14) * mm, "end": v(195.6, -0.3) * mm});
            skLineSegment(sketch, "E478", {"start": v(195.6, -0.3) * mm, "end": v(195.6, 1.8) * mm});
            skLineSegment(sketch, "E479", {"start": v(195.6, 1.8) * mm, "end": v(195.96, 8.12) * mm});
            skLineSegment(sketch, "E480", {"start": v(195.96, 8.12) * mm, "end": v(197.05, 16.13) * mm});
            skLineSegment(sketch, "E481", {"start": v(197.05, 16.13) * mm, "end": v(198.86, 23.7) * mm});
            skLineSegment(sketch, "E482", {"start": v(198.86, 23.7) * mm, "end": v(201.4, 30.85) * mm});
            skLineSegment(sketch, "E483", {"start": v(201.4, 30.85) * mm, "end": v(204.65, 37.56) * mm});
            skLineSegment(sketch, "E484", {"start": v(204.65, 37.56) * mm, "end": v(208.62, 43.84) * mm});
            skLineSegment(sketch, "E485", {"start": v(208.62, 43.84) * mm, "end": v(213.3, 49.66) * mm});
            skLineSegment(sketch, "E486", {"start": v(213.3, 49.66) * mm, "end": v(217.27, 53.76) * mm});
            skLineSegment(sketch, "E487", {"start": v(217.27, 53.76) * mm, "end": v(218.69, 55.02) * mm});
            skLineSegment(sketch, "E488", {"start": v(218.69, 55.02) * mm, "end": v(220.38, 56.53) * mm});
            skLineSegment(sketch, "E489", {"start": v(220.38, 56.53) * mm, "end": v(225.83, 60.64) * mm});
            skLineSegment(sketch, "E490", {"start": v(225.83, 60.64) * mm, "end": v(233.73, 65.48) * mm});
            skLineSegment(sketch, "E491", {"start": v(233.73, 65.48) * mm, "end": v(242.3, 69.49) * mm});
            skLineSegment(sketch, "E492", {"start": v(242.3, 69.49) * mm, "end": v(251.42, 72.65) * mm});
            skLineSegment(sketch, "E493", {"start": v(251.42, 72.65) * mm, "end": v(261, 74.93) * mm});
            skLineSegment(sketch, "E494", {"start": v(261, 74.93) * mm, "end": v(270.93, 76.3) * mm});
            skLineSegment(sketch, "E495", {"start": v(270.93, 76.3) * mm, "end": v(281.1, 76.74) * mm});
            skLineSegment(sketch, "E496", {"start": v(281.1, 76.74) * mm, "end": v(288.86, 76.45) * mm});
            skLineSegment(sketch, "E497", {"start": v(288.86, 76.45) * mm, "end": v(291.43, 76.2) * mm});
            skLineSegment(sketch, "E498", {"start": v(291.43, 76.2) * mm, "end": v(293.87, 75.96) * mm});
            skLineSegment(sketch, "E499", {"start": v(293.87, 75.96) * mm, "end": v(301.12, 74.63) * mm});
            skLineSegment(sketch, "E500", {"start": v(301.12, 74.63) * mm, "end": v(310.1, 72.09) * mm});
            skLineSegment(sketch, "E501", {"start": v(310.1, 72.09) * mm, "end": v(318.26, 68.85) * mm});
            skLineSegment(sketch, "E502", {"start": v(318.26, 68.85) * mm, "end": v(325.56, 65.2) * mm});
            skLineSegment(sketch, "E503", {"start": v(325.56, 65.2) * mm, "end": v(331.9, 61.42) * mm});
            skLineSegment(sketch, "E504", {"start": v(331.9, 61.42) * mm, "end": v(337.23, 57.8) * mm});
            skLineSegment(sketch, "E505", {"start": v(337.23, 57.8) * mm, "end": v(341.46, 54.64) * mm});
            skLineSegment(sketch, "E506", {"start": v(341.46, 54.64) * mm, "end": v(343.75, 52.81) * mm});
            skLineSegment(sketch, "E507", {"start": v(343.75, 52.81) * mm, "end": v(344.5, 52.2) * mm});
            skLineSegment(sketch, "E508", {"start": v(344.5, 52.2) * mm, "end": v(344.72, 52.01) * mm});
            skLineSegment(sketch, "E509", {"start": v(344.72, 52.01) * mm, "end": v(345.27, 51.54) * mm});
            skLineSegment(sketch, "E510", {"start": v(345.27, 51.54) * mm, "end": v(346.05, 50.86) * mm});
            skLineSegment(sketch, "E511", {"start": v(346.05, 50.86) * mm, "end": v(346.94, 50.08) * mm});
            skLineSegment(sketch, "E512", {"start": v(346.94, 50.08) * mm, "end": v(347.84, 49.3) * mm});
            skLineSegment(sketch, "E513", {"start": v(347.84, 49.3) * mm, "end": v(348.62, 48.62) * mm});
            skLineSegment(sketch, "E514", {"start": v(348.62, 48.62) * mm, "end": v(349.19, 48.13) * mm});
            skLineSegment(sketch, "E515", {"start": v(349.19, 48.13) * mm, "end": v(349.4, 47.95) * mm});
            skLineSegment(sketch, "E516", {"start": v(349.4, 47.95) * mm, "end": v(349.41, 47.93) * mm});
            skLineSegment(sketch, "E517", {"start": v(349.41, 47.93) * mm, "end": v(358.95, 39.66) * mm});
            skLineSegment(sketch, "E518", {"start": v(358.95, 39.66) * mm, "end": v(360.24, 39.18) * mm});
            skLineSegment(sketch, "E519", {"start": v(360.24, 39.18) * mm, "end": v(378.7, 39.18) * mm});
            skLineSegment(sketch, "E520", {"start": v(378.7, 39.18) * mm, "end": v(378.83, 39.18) * mm});
            skLineSegment(sketch, "E521", {"start": v(378.83, 39.18) * mm, "end": v(379.22, 39.28) * mm});
            skLineSegment(sketch, "E522", {"start": v(379.22, 39.28) * mm, "end": v(379.64, 39.56) * mm});
            skLineSegment(sketch, "E523", {"start": v(379.64, 39.56) * mm, "end": v(379.93, 39.97) * mm});
            skLineSegment(sketch, "E524", {"start": v(379.93, 39.97) * mm, "end": v(380.03, 40.35) * mm});
            skLineSegment(sketch, "E525", {"start": v(380.03, 40.35) * mm, "end": v(380.03, 40.47) * mm});
            skLineSegment(sketch, "E526", {"start": v(380.03, 40.47) * mm, "end": v(380.03, 105.84) * mm});
            skLineSegment(sketch, "E527", {"start": v(380.03, 105.84) * mm, "end": v(380.03, 105.96) * mm});
            skLineSegment(sketch, "E528", {"start": v(380.03, 105.96) * mm, "end": v(379.93, 106.34) * mm});
            skLineSegment(sketch, "E529", {"start": v(379.93, 106.34) * mm, "end": v(379.64, 106.75) * mm});
            skLineSegment(sketch, "E530", {"start": v(379.64, 106.75) * mm, "end": v(379.22, 107.03) * mm});
            skLineSegment(sketch, "E531", {"start": v(379.22, 107.03) * mm, "end": v(378.83, 107.13) * mm});
            skLineSegment(sketch, "E532", {"start": v(378.83, 107.13) * mm, "end": v(378.7, 107.13) * mm});
            skLineSegment(sketch, "E533", {"start": v(378.7, 107.13) * mm, "end": v(344.54, 107.13) * mm});
            skLineSegment(sketch, "E534", {"start": v(344.54, 107.13) * mm, "end": v(344.54, 92.68) * mm});
            skLineSegment(sketch, "E535", {"start": v(344.54, 92.68) * mm, "end": v(342.67, 93.7) * mm});
            skLineSegment(sketch, "E536", {"start": v(342.67, 93.7) * mm, "end": v(341.54, 94.32) * mm});
            skLineSegment(sketch, "E537", {"start": v(341.54, 94.32) * mm, "end": v(338.13, 96.11) * mm});
            skLineSegment(sketch, "E538", {"start": v(338.13, 96.11) * mm, "end": v(333.18, 98.55) * mm});
            skLineSegment(sketch, "E539", {"start": v(333.18, 98.55) * mm, "end": v(327.82, 100.95) * mm});
            skLineSegment(sketch, "E540", {"start": v(327.82, 100.95) * mm, "end": v(322.05, 103.23) * mm});
            skLineSegment(sketch, "E541", {"start": v(322.05, 103.23) * mm, "end": v(315.86, 105.3) * mm});
            skLineSegment(sketch, "E542", {"start": v(315.86, 105.3) * mm, "end": v(309.26, 107.09) * mm});
            skLineSegment(sketch, "E543", {"start": v(309.26, 107.09) * mm, "end": v(302.23, 108.52) * mm});
            skLineSegment(sketch, "E544", {"start": v(302.23, 108.52) * mm, "end": v(296.65, 109.33) * mm});
            skLineSegment(sketch, "E545", {"start": v(296.65, 109.33) * mm, "end": v(294.78, 109.5) * mm});
            skLineSegment(sketch, "E546", {"start": v(294.78, 109.5) * mm, "end": v(293.61, 109.63) * mm});
            skLineSegment(sketch, "E547", {"start": v(293.61, 109.63) * mm, "end": v(283.97, 110.2) * mm});
            skLineSegment(sketch, "E548", {"start": v(283.97, 110.2) * mm, "end": v(280.75, 110.2) * mm});
            skLineSegment(sketch, "E549", {"start": v(280.75, 110.2) * mm, "end": v(277.76, 110.2) * mm});
            skLineSegment(sketch, "E550", {"start": v(277.76, 110.2) * mm, "end": v(268.78, 109.7) * mm});
            skLineSegment(sketch, "E551", {"start": v(268.78, 109.7) * mm, "end": v(257, 108.2) * mm});
            skLineSegment(sketch, "E552", {"start": v(257, 108.2) * mm, "end": v(245.52, 105.72) * mm});
            skLineSegment(sketch, "E553", {"start": v(245.52, 105.72) * mm, "end": v(234.43, 102.3) * mm});
            skLineSegment(sketch, "E554", {"start": v(234.43, 102.3) * mm, "end": v(223.84, 97.99) * mm});
            skLineSegment(sketch, "E555", {"start": v(223.84, 97.99) * mm, "end": v(213.81, 92.78) * mm});
            skLineSegment(sketch, "E556", {"start": v(213.81, 92.78) * mm, "end": v(204.47, 86.71) * mm});
            skLineSegment(sketch, "E557", {"start": v(204.47, 86.71) * mm, "end": v(197.93, 81.65) * mm});
            skLineSegment(sketch, "E558", {"start": v(197.93, 81.65) * mm, "end": v(195.88, 79.82) * mm});
            skLineSegment(sketch, "E559", {"start": v(195.88, 79.82) * mm, "end": v(193.8, 77.97) * mm});
            skLineSegment(sketch, "E560", {"start": v(193.8, 77.97) * mm, "end": v(187.98, 71.96) * mm});
            skLineSegment(sketch, "E561", {"start": v(187.98, 71.96) * mm, "end": v(181.08, 63.41) * mm});
            skLineSegment(sketch, "E562", {"start": v(181.08, 63.41) * mm, "end": v(175.2, 54.21) * mm});
            skLineSegment(sketch, "E563", {"start": v(175.2, 54.21) * mm, "end": v(170.36, 44.4) * mm});
            skLineSegment(sketch, "E564", {"start": v(170.36, 44.4) * mm, "end": v(166.57, 34) * mm});
            skLineSegment(sketch, "E565", {"start": v(166.57, 34) * mm, "end": v(163.84, 23.05) * mm});
            skLineSegment(sketch, "E566", {"start": v(163.84, 23.05) * mm, "end": v(162.19, 11.6) * mm});
            skLineSegment(sketch, "E567", {"start": v(162.19, 11.6) * mm, "end": v(161.63, 2.64) * mm});
            skLineSegment(sketch, "E568", {"start": v(161.63, 2.64) * mm, "end": v(161.63, -0.34) * mm});
            skLineSegment(sketch, "E569", {"start": v(-287.9, -17.8) * mm, "end": v(-262.66, 47.2) * mm});
            skLineSegment(sketch, "E570", {"start": v(-262.66, 47.2) * mm, "end": v(-251.97, 74.73) * mm});
            skLineSegment(sketch, "E571", {"start": v(-251.97, 74.73) * mm, "end": v(-250.85, 74.73) * mm});
            skLineSegment(sketch, "E572", {"start": v(-250.85, 74.73) * mm, "end": v(-240.15, 47.2) * mm});
            skLineSegment(sketch, "E573", {"start": v(-240.15, 47.2) * mm, "end": v(-214.9, -17.8) * mm});
            skLineSegment(sketch, "E574", {"start": v(-214.9, -17.8) * mm, "end": v(-287.9, -17.8) * mm});
            skLineSegment(sketch, "E575", {"start": v(-147.43, -103.8) * mm, "end": v(-158.71, -74.75) * mm});
            skLineSegment(sketch, "E576", {"start": v(-158.71, -74.75) * mm, "end": v(-216.78, 74.74) * mm});
            skLineSegment(sketch, "E577", {"start": v(-216.78, 74.74) * mm, "end": v(-229.36, 107.13) * mm});
            skLineSegment(sketch, "E578", {"start": v(-229.36, 107.13) * mm, "end": v(-251.4, 107.13) * mm});
            skLineSegment(sketch, "E579", {"start": v(-251.4, 107.13) * mm, "end": v(-273.45, 107.13) * mm});
            skLineSegment(sketch, "E580", {"start": v(-273.45, 107.13) * mm, "end": v(-273.45, 107.13) * mm});
            skLineSegment(sketch, "E581", {"start": v(-273.45, 107.13) * mm, "end": v(-299.83, 107.13) * mm});
            skLineSegment(sketch, "E582", {"start": v(-299.83, 107.13) * mm, "end": v(-299.98, 107.13) * mm});
            skLineSegment(sketch, "E583", {"start": v(-299.98, 107.13) * mm, "end": v(-300.44, 106.98) * mm});
            skLineSegment(sketch, "E584", {"start": v(-300.44, 106.98) * mm, "end": v(-300.85, 106.67) * mm});
            skLineSegment(sketch, "E585", {"start": v(-300.85, 106.67) * mm, "end": v(-300.9, 106.59) * mm});
            skLineSegment(sketch, "E586", {"start": v(-300.9, 106.59) * mm, "end": v(-300.97, 106.5) * mm});
            skLineSegment(sketch, "E587", {"start": v(-300.97, 106.5) * mm, "end": v(-301.14, 106.02) * mm});
            skLineSegment(sketch, "E588", {"start": v(-301.14, 106.02) * mm, "end": v(-301.13, 105.51) * mm});
            skLineSegment(sketch, "E589", {"start": v(-301.13, 105.51) * mm, "end": v(-301.1, 105.41) * mm});
            skLineSegment(sketch, "E590", {"start": v(-301.1, 105.41) * mm, "end": v(-290.64, 74.73) * mm});
            skLineSegment(sketch, "E591", {"start": v(-290.64, 74.73) * mm, "end": v(-286.03, 74.73) * mm});
            skLineSegment(sketch, "E592", {"start": v(-286.03, 74.73) * mm, "end": v(-344.1, -74.75) * mm});
            skLineSegment(sketch, "E593", {"start": v(-344.1, -74.75) * mm, "end": v(-344.1, -74.75) * mm});
            skLineSegment(sketch, "E594", {"start": v(-344.1, -74.75) * mm, "end": v(-349.7, -74.76) * mm});
            skLineSegment(sketch, "E595", {"start": v(-349.7, -74.76) * mm, "end": v(-359.9, -104.74) * mm});
            skLineSegment(sketch, "E596", {"start": v(-359.9, -104.74) * mm, "end": v(-359.95, -104.88) * mm});
            skLineSegment(sketch, "E597", {"start": v(-359.95, -104.88) * mm, "end": v(-359.98, -105.6) * mm});
            skLineSegment(sketch, "E598", {"start": v(-359.98, -105.6) * mm, "end": v(-359.74, -106.27) * mm});
            skLineSegment(sketch, "E599", {"start": v(-359.74, -106.27) * mm, "end": v(-359.64, -106.39) * mm});
            skLineSegment(sketch, "E600", {"start": v(-359.64, -106.39) * mm, "end": v(-359.55, -106.51) * mm});
            skLineSegment(sketch, "E601", {"start": v(-359.55, -106.51) * mm, "end": v(-358.98, -106.95) * mm});
            skLineSegment(sketch, "E602", {"start": v(-358.98, -106.95) * mm, "end": v(-358.33, -107.15) * mm});
            skLineSegment(sketch, "E603", {"start": v(-358.33, -107.15) * mm, "end": v(-358.12, -107.15) * mm});
            skLineSegment(sketch, "E604", {"start": v(-358.12, -107.15) * mm, "end": v(-343.83, -107.16) * mm});
            skLineSegment(sketch, "E605", {"start": v(-343.83, -107.16) * mm, "end": v(-343.83, -107.15) * mm});
            skLineSegment(sketch, "E606", {"start": v(-343.83, -107.15) * mm, "end": v(-323.99, -107.15) * mm});
            skLineSegment(sketch, "E607", {"start": v(-323.99, -107.15) * mm, "end": v(-323.85, -107.15) * mm});
            skLineSegment(sketch, "E608", {"start": v(-323.85, -107.15) * mm, "end": v(-323.42, -107.05) * mm});
            skLineSegment(sketch, "E609", {"start": v(-323.42, -107.05) * mm, "end": v(-322.87, -106.77) * mm});
            skLineSegment(sketch, "E610", {"start": v(-322.87, -106.77) * mm, "end": v(-322.42, -106.36) * mm});
            skLineSegment(sketch, "E611", {"start": v(-322.42, -106.36) * mm, "end": v(-322.17, -105.99) * mm});
            skLineSegment(sketch, "E612", {"start": v(-322.17, -105.99) * mm, "end": v(-322.11, -105.85) * mm});
            skLineSegment(sketch, "E613", {"start": v(-322.11, -105.85) * mm, "end": v(-300.48, -50.16) * mm});
            skLineSegment(sketch, "E614", {"start": v(-300.48, -50.16) * mm, "end": v(-202.33, -50.16) * mm});
            skLineSegment(sketch, "E615", {"start": v(-202.33, -50.16) * mm, "end": v(-180.7, -105.85) * mm});
            skLineSegment(sketch, "E616", {"start": v(-180.7, -105.85) * mm, "end": v(-180.65, -105.99) * mm});
            skLineSegment(sketch, "E617", {"start": v(-180.65, -105.99) * mm, "end": v(-180.39, -106.36) * mm});
            skLineSegment(sketch, "E618", {"start": v(-180.39, -106.36) * mm, "end": v(-179.91, -106.77) * mm});
            skLineSegment(sketch, "E619", {"start": v(-179.91, -106.77) * mm, "end": v(-179.34, -107.05) * mm});
            skLineSegment(sketch, "E620", {"start": v(-179.34, -107.05) * mm, "end": v(-178.88, -107.15) * mm});
            skLineSegment(sketch, "E621", {"start": v(-178.88, -107.15) * mm, "end": v(-178.73, -107.15) * mm});
            skLineSegment(sketch, "E622", {"start": v(-178.73, -107.15) * mm, "end": v(-149.88, -107.15) * mm});
            skLineSegment(sketch, "E623", {"start": v(-149.88, -107.15) * mm, "end": v(-149.57, -107.15) * mm});
            skLineSegment(sketch, "E624", {"start": v(-149.57, -107.15) * mm, "end": v(-148.64, -106.85) * mm});
            skLineSegment(sketch, "E625", {"start": v(-148.64, -106.85) * mm, "end": v(-147.74, -106.08) * mm});
            skLineSegment(sketch, "E626", {"start": v(-147.74, -106.08) * mm, "end": v(-147.3, -105) * mm});
            skLineSegment(sketch, "E627", {"start": v(-147.3, -105) * mm, "end": v(-147.32, -104.07) * mm});
            skLineSegment(sketch, "E628", {"start": v(-147.32, -104.07) * mm, "end": v(-147.43, -103.8) * mm});
            skLineSegment(sketch, "E629", {"start": v(127.86, 106.6) * mm, "end": v(127.8, 106.68) * mm});
            skLineSegment(sketch, "E630", {"start": v(127.8, 106.68) * mm, "end": v(127.4, 106.99) * mm});
            skLineSegment(sketch, "E631", {"start": v(127.4, 106.99) * mm, "end": v(126.95, 107.13) * mm});
            skLineSegment(sketch, "E632", {"start": v(126.95, 107.13) * mm, "end": v(126.8, 107.13) * mm});
            skLineSegment(sketch, "E633", {"start": v(126.8, 107.13) * mm, "end": v(80.98, 107.12) * mm});
            skLineSegment(sketch, "E634", {"start": v(80.98, 107.12) * mm, "end": v(80.86, 107.12) * mm});
            skLineSegment(sketch, "E635", {"start": v(80.86, 107.12) * mm, "end": v(80.47, 107.02) * mm});
            skLineSegment(sketch, "E636", {"start": v(80.47, 107.02) * mm, "end": v(80.06, 106.74) * mm});
            skLineSegment(sketch, "E637", {"start": v(80.06, 106.74) * mm, "end": v(79.78, 106.33) * mm});
            skLineSegment(sketch, "E638", {"start": v(79.78, 106.33) * mm, "end": v(79.68, 105.95) * mm});
            skLineSegment(sketch, "E639", {"start": v(79.68, 105.95) * mm, "end": v(79.68, 105.83) * mm});
            skLineSegment(sketch, "E640", {"start": v(79.68, 105.83) * mm, "end": v(79.68, -49.2) * mm});
            skLineSegment(sketch, "E641", {"start": v(79.68, -49.2) * mm, "end": v(79.68, -49.48) * mm});
            skLineSegment(sketch, "E642", {"start": v(79.68, -49.48) * mm, "end": v(79.5, -50.35) * mm});
            skLineSegment(sketch, "E643", {"start": v(79.5, -50.35) * mm, "end": v(79, -51.37) * mm});
            skLineSegment(sketch, "E644", {"start": v(79, -51.37) * mm, "end": v(78.23, -52.2) * mm});
            skLineSegment(sketch, "E645", {"start": v(78.23, -52.2) * mm, "end": v(77.5, -52.67) * mm});
            skLineSegment(sketch, "E646", {"start": v(77.5, -52.67) * mm, "end": v(77.22, -52.77) * mm});
            skLineSegment(sketch, "E647", {"start": v(77.22, -52.77) * mm, "end": v(76.95, -52.87) * mm});
            skLineSegment(sketch, "E648", {"start": v(76.95, -52.87) * mm, "end": v(76.08, -53.02) * mm});
            skLineSegment(sketch, "E649", {"start": v(76.08, -53.02) * mm, "end": v(74.96, -52.93) * mm});
            skLineSegment(sketch, "E650", {"start": v(74.96, -52.93) * mm, "end": v(73.9, -52.5) * mm});
            skLineSegment(sketch, "E651", {"start": v(73.9, -52.5) * mm, "end": v(73.2, -51.98) * mm});
            skLineSegment(sketch, "E652", {"start": v(73.2, -51.98) * mm, "end": v(73, -51.77) * mm});
            skLineSegment(sketch, "E653", {"start": v(73, -51.77) * mm, "end": v(-66.67, 107.12) * mm});
            skLineSegment(sketch, "E654", {"start": v(-66.67, 107.12) * mm, "end": v(-112.32, 107.13) * mm});
            skLineSegment(sketch, "E655", {"start": v(-112.32, 107.13) * mm, "end": v(-112.47, 107.13) * mm});
            skLineSegment(sketch, "E656", {"start": v(-112.47, 107.13) * mm, "end": v(-112.92, 106.99) * mm});
            skLineSegment(sketch, "E657", {"start": v(-112.92, 106.99) * mm, "end": v(-113.31, 106.68) * mm});
            skLineSegment(sketch, "E658", {"start": v(-113.31, 106.68) * mm, "end": v(-113.38, 106.6) * mm});
            skLineSegment(sketch, "E659", {"start": v(-113.38, 106.6) * mm, "end": v(-113.44, 106.5) * mm});
            skLineSegment(sketch, "E660", {"start": v(-113.44, 106.5) * mm, "end": v(-113.6, 106.02) * mm});
            skLineSegment(sketch, "E661", {"start": v(-113.6, 106.02) * mm, "end": v(-113.59, 105.52) * mm});
            skLineSegment(sketch, "E662", {"start": v(-113.59, 105.52) * mm, "end": v(-113.56, 105.41) * mm});
            skLineSegment(sketch, "E663", {"start": v(-113.56, 105.41) * mm, "end": v(-103.33, 74.74) * mm});
            skLineSegment(sketch, "E664", {"start": v(-103.33, 74.74) * mm, "end": v(-97.6, 74.74) * mm});
            skLineSegment(sketch, "E665", {"start": v(-97.6, 74.74) * mm, "end": v(-97.6, -74.75) * mm});
            skLineSegment(sketch, "E666", {"start": v(-97.6, -74.75) * mm, "end": v(-103.32, -74.75) * mm});
            skLineSegment(sketch, "E667", {"start": v(-103.32, -74.75) * mm, "end": v(-113.31, -104.73) * mm});
            skLineSegment(sketch, "E668", {"start": v(-113.31, -104.73) * mm, "end": v(-113.37, -104.87) * mm});
            skLineSegment(sketch, "E669", {"start": v(-113.37, -104.87) * mm, "end": v(-113.4, -105.59) * mm});
            skLineSegment(sketch, "E670", {"start": v(-113.4, -105.59) * mm, "end": v(-113.15, -106.26) * mm});
            skLineSegment(sketch, "E671", {"start": v(-113.15, -106.26) * mm, "end": v(-113.07, -106.39) * mm});
            skLineSegment(sketch, "E672", {"start": v(-113.07, -106.39) * mm, "end": v(-112.98, -106.5) * mm});
            skLineSegment(sketch, "E673", {"start": v(-112.98, -106.5) * mm, "end": v(-112.41, -106.95) * mm});
            skLineSegment(sketch, "E674", {"start": v(-112.41, -106.95) * mm, "end": v(-111.79, -107.15) * mm});
            skLineSegment(sketch, "E675", {"start": v(-111.79, -107.15) * mm, "end": v(-111.58, -107.15) * mm});
            skLineSegment(sketch, "E676", {"start": v(-111.58, -107.15) * mm, "end": v(-66.5, -107.16) * mm});
            skLineSegment(sketch, "E677", {"start": v(-66.5, -107.16) * mm, "end": v(-66.38, -107.16) * mm});
            skLineSegment(sketch, "E678", {"start": v(-66.38, -107.16) * mm, "end": v(-66, -107.05) * mm});
            skLineSegment(sketch, "E679", {"start": v(-66, -107.05) * mm, "end": v(-65.58, -106.77) * mm});
            skLineSegment(sketch, "E680", {"start": v(-65.58, -106.77) * mm, "end": v(-65.3, -106.36) * mm});
            skLineSegment(sketch, "E681", {"start": v(-65.3, -106.36) * mm, "end": v(-65.2, -105.98) * mm});
            skLineSegment(sketch, "E682", {"start": v(-65.2, -105.98) * mm, "end": v(-65.2, -105.85) * mm});
            skLineSegment(sketch, "E683", {"start": v(-65.2, -105.85) * mm, "end": v(-65.2, 46.65) * mm});
            skLineSegment(sketch, "E684", {"start": v(-65.2, 46.65) * mm, "end": v(-65.2, 46.94) * mm});
            skLineSegment(sketch, "E685", {"start": v(-65.2, 46.94) * mm, "end": v(-65.03, 47.8) * mm});
            skLineSegment(sketch, "E686", {"start": v(-65.03, 47.8) * mm, "end": v(-64.53, 48.82) * mm});
            skLineSegment(sketch, "E687", {"start": v(-64.53, 48.82) * mm, "end": v(-63.76, 49.65) * mm});
            skLineSegment(sketch, "E688", {"start": v(-63.76, 49.65) * mm, "end": v(-63.01, 50.12) * mm});
            skLineSegment(sketch, "E689", {"start": v(-63.01, 50.12) * mm, "end": v(-62.74, 50.23) * mm});
            skLineSegment(sketch, "E690", {"start": v(-62.74, 50.23) * mm, "end": v(-62.47, 50.33) * mm});
            skLineSegment(sketch, "E691", {"start": v(-62.47, 50.33) * mm, "end": v(-61.6, 50.48) * mm});
            skLineSegment(sketch, "E692", {"start": v(-61.6, 50.48) * mm, "end": v(-60.48, 50.39) * mm});
            skLineSegment(sketch, "E693", {"start": v(-60.48, 50.39) * mm, "end": v(-59.43, 49.96) * mm});
            skLineSegment(sketch, "E694", {"start": v(-59.43, 49.96) * mm, "end": v(-58.72, 49.44) * mm});
            skLineSegment(sketch, "E695", {"start": v(-58.72, 49.44) * mm, "end": v(-58.53, 49.22) * mm});
            skLineSegment(sketch, "E696", {"start": v(-58.53, 49.22) * mm, "end": v(78.12, -106.22) * mm});
            skLineSegment(sketch, "E697", {"start": v(78.12, -106.22) * mm, "end": v(78.26, -106.37) * mm});
            skLineSegment(sketch, "E698", {"start": v(78.26, -106.37) * mm, "end": v(79.07, -106.9) * mm});
            skLineSegment(sketch, "E699", {"start": v(79.07, -106.9) * mm, "end": v(79.93, -107.15) * mm});
            skLineSegment(sketch, "E700", {"start": v(79.93, -107.15) * mm, "end": v(80.22, -107.15) * mm});
            skLineSegment(sketch, "E701", {"start": v(80.22, -107.15) * mm, "end": v(109.26, -107.15) * mm});
            skLineSegment(sketch, "E702", {"start": v(109.26, -107.15) * mm, "end": v(109.53, -107.15) * mm});
            skLineSegment(sketch, "E703", {"start": v(109.53, -107.15) * mm, "end": v(110.35, -106.93) * mm});
            skLineSegment(sketch, "E704", {"start": v(110.35, -106.93) * mm, "end": v(111.24, -106.32) * mm});
            skLineSegment(sketch, "E705", {"start": v(111.24, -106.32) * mm, "end": v(111.85, -105.43) * mm});
            skLineSegment(sketch, "E706", {"start": v(111.85, -105.43) * mm, "end": v(112.07, -104.6) * mm});
            skLineSegment(sketch, "E707", {"start": v(112.07, -104.6) * mm, "end": v(112.07, -104.34) * mm});
            skLineSegment(sketch, "E708", {"start": v(112.07, -104.34) * mm, "end": v(112.07, 74.74) * mm});
            skLineSegment(sketch, "E709", {"start": v(112.07, 74.74) * mm, "end": v(117.81, 74.74) * mm});
            skLineSegment(sketch, "E710", {"start": v(117.81, 74.74) * mm, "end": v(128.03, 105.41) * mm});
            skLineSegment(sketch, "E711", {"start": v(128.03, 105.41) * mm, "end": v(128.06, 105.52) * mm});
            skLineSegment(sketch, "E712", {"start": v(128.06, 105.52) * mm, "end": v(128.09, 106.02) * mm});
            skLineSegment(sketch, "E713", {"start": v(128.09, 106.02) * mm, "end": v(127.92, 106.5) * mm});
            skLineSegment(sketch, "E714", {"start": v(127.92, 106.5) * mm, "end": v(127.86, 106.6) * mm});
            skSolve(sketch);
        }
        {
            var Q0;
            Q0 = qSketchRegion(id + "F0", true);
            var Q1;
            Q1=makeQuery(id+"F0.imprint","IMPRINT",FACE,{"disambiguationData":[TD([[makeQuery(id+"F0.imprint","IMPRINT",EDGE,{"derivedFrom":sQuery(id+"F0.wireOp",EDGE,"E48")}),-1.0]])]});
            var Q2;
            Q2=makeQuery(id+"F0.imprint","IMPRINT",FACE,{"disambiguationData":[TD([[makeQuery(id+"F0.imprint","IMPRINT",EDGE,{"derivedFrom":sQuery(id+"F0.wireOp",EDGE,"E48")}),1.0]])]});
            var Q3;
            Q3=makeQuery(id+"F0.imprint","IMPRINT",FACE,{"disambiguationData":[TD([[makeQuery(id+"F0.imprint","IMPRINT",EDGE,{"derivedFrom":sQuery(id+"F0.wireOp",EDGE,"E357")}),1.0]])]});
            var Q4;
            Q4=makeQuery(id+"F0.imprint","IMPRINT",FACE,{"disambiguationData":[TD([[makeQuery(id+"F0.imprint","IMPRINT",EDGE,{"derivedFrom":sQuery(id+"F0.wireOp",EDGE,"E629")}),1.0]])]});
            var Q5;
            Q5=makeQuery(id+"F0.imprint","IMPRINT",FACE,{"disambiguationData":[TD([[makeQuery(id+"F0.imprint","IMPRINT",EDGE,{"derivedFrom":sQuery(id+"F0.wireOp",EDGE,"E569")}),-1.0]])]});
            var Q6;
            Q6=makeQuery(id+"F0.imprint","IMPRINT",FACE,{"disambiguationData":[TD([[makeQuery(id+"F0.imprint","IMPRINT",EDGE,{"derivedFrom":sQuery(id+"F0.wireOp",EDGE,"E569")}),1.0]])]});
            var Q7;
            Q7=makeQuery(id+"F0.imprint","IMPRINT",FACE,{"disambiguationData":[TD([[makeQuery(id+"F0.imprint","IMPRINT",EDGE,{"derivedFrom":sQuery(id+"F0.wireOp",EDGE,"E184")}),1.0]])]});
            var Q8;
            Q8=makeQuery(id+"F0.imprint","IMPRINT",FACE,{"disambiguationData":[TD([[makeQuery(id+"F0.imprint","IMPRINT",EDGE,{"derivedFrom":sQuery(id+"F0.wireOp",EDGE,"E184")}),-1.0]])]});
            extrude(context, id + "F1", {"entities" : qUnion([Q0, Q1, Q2, Q3, Q4, Q5, Q6, Q7, Q8]), "oppositeDirection" : true, "depth" : 6.35 * mm, "offsetDistance" : 25.4 * mm});
        }
        {
            var Q0;
            Q0=makeQuery(id+"F0.imprint","IMPRINT",FACE,{"disambiguationData":[TD([[makeQuery(id+"F0.imprint","IMPRINT",EDGE,{"derivedFrom":sQuery(id+"F0.wireOp",EDGE,"E184")}),1.0]])]});
            var Q1;
            Q1=makeQuery(id+"F0.imprint","IMPRINT",FACE,{"disambiguationData":[TD([[makeQuery(id+"F0.imprint","IMPRINT",EDGE,{"derivedFrom":sQuery(id+"F0.wireOp",EDGE,"E569")}),1.0]])]});
            var Q2;
            Q2=makeQuery(id+"F0.imprint","IMPRINT",FACE,{"disambiguationData":[TD([[makeQuery(id+"F0.imprint","IMPRINT",EDGE,{"derivedFrom":sQuery(id+"F0.wireOp",EDGE,"E629")}),1.0]])]});
            var Q3;
            Q3=makeQuery(id+"F0.imprint","IMPRINT",FACE,{"disambiguationData":[TD([[makeQuery(id+"F0.imprint","IMPRINT",EDGE,{"derivedFrom":sQuery(id+"F0.wireOp",EDGE,"E357")}),1.0]])]});
            var Q4;
            Q4=makeQuery(id+"F0.imprint","IMPRINT",FACE,{"disambiguationData":[TD([[makeQuery(id+"F0.imprint","IMPRINT",EDGE,{"derivedFrom":sQuery(id+"F0.wireOp",EDGE,"E48")}),1.0]])]});
            extrude(context, id + "F2", {"entities" : qUnion([Q0, Q1, Q2, Q3, Q4]), "depth" : 76.2 * mm, "offsetDistance" : 25.4 * mm});
        }
        {
            var Q0;
            Q0=makeQuery(id+"F2.opExtrude","CAP_FACE",FACE,{"disambiguationData":[OSD([sQuery(id+"F0.wireOp",EDGE,"E569"),sQuery(id+"F0.wireOp",EDGE,"E570"),sQuery(id+"F0.wireOp",EDGE,"E571"),sQuery(id+"F0.wireOp",EDGE,"E572"),sQuery(id+"F0.wireOp",EDGE,"E573"),sQuery(id+"F0.wireOp",EDGE,"E574"),sQuery(id+"F0.wireOp",EDGE,"E575"),sQuery(id+"F0.wireOp",EDGE,"E576"),sQuery(id+"F0.wireOp",EDGE,"E577"),sQuery(id+"F0.wireOp",EDGE,"E578"),sQuery(id+"F0.wireOp",EDGE,"E579"),sQuery(id+"F0.wireOp",EDGE,"E580"),sQuery(id+"F0.wireOp",EDGE,"E581"),sQuery(id+"F0.wireOp",EDGE,"E582"),sQuery(id+"F0.wireOp",EDGE,"E583"),sQuery(id+"F0.wireOp",EDGE,"E584"),sQuery(id+"F0.wireOp",EDGE,"E585"),sQuery(id+"F0.wireOp",EDGE,"E586"),sQuery(id+"F0.wireOp",EDGE,"E587"),sQuery(id+"F0.wireOp",EDGE,"E588"),sQuery(id+"F0.wireOp",EDGE,"E589"),sQuery(id+"F0.wireOp",EDGE,"E590"),sQuery(id+"F0.wireOp",EDGE,"E591"),sQuery(id+"F0.wireOp",EDGE,"E592"),sQuery(id+"F0.wireOp",EDGE,"E593"),sQuery(id+"F0.wireOp",EDGE,"E594"),sQuery(id+"F0.wireOp",EDGE,"E595"),sQuery(id+"F0.wireOp",EDGE,"E596"),sQuery(id+"F0.wireOp",EDGE,"E597"),sQuery(id+"F0.wireOp",EDGE,"E598"),sQuery(id+"F0.wireOp",EDGE,"E599"),sQuery(id+"F0.wireOp",EDGE,"E600"),sQuery(id+"F0.wireOp",EDGE,"E601"),sQuery(id+"F0.wireOp",EDGE,"E602"),sQuery(id+"F0.wireOp",EDGE,"E603"),sQuery(id+"F0.wireOp",EDGE,"E604"),sQuery(id+"F0.wireOp",EDGE,"E605"),sQuery(id+"F0.wireOp",EDGE,"E606"),sQuery(id+"F0.wireOp",EDGE,"E607"),sQuery(id+"F0.wireOp",EDGE,"E608"),sQuery(id+"F0.wireOp",EDGE,"E609"),sQuery(id+"F0.wireOp",EDGE,"E610"),sQuery(id+"F0.wireOp",EDGE,"E611"),sQuery(id+"F0.wireOp",EDGE,"E612"),sQuery(id+"F0.wireOp",EDGE,"E613"),sQuery(id+"F0.wireOp",EDGE,"E614"),sQuery(id+"F0.wireOp",EDGE,"E615"),sQuery(id+"F0.wireOp",EDGE,"E616"),sQuery(id+"F0.wireOp",EDGE,"E617"),sQuery(id+"F0.wireOp",EDGE,"E618"),sQuery(id+"F0.wireOp",EDGE,"E619"),sQuery(id+"F0.wireOp",EDGE,"E620"),sQuery(id+"F0.wireOp",EDGE,"E621"),sQuery(id+"F0.wireOp",EDGE,"E622"),sQuery(id+"F0.wireOp",EDGE,"E623"),sQuery(id+"F0.wireOp",EDGE,"E624"),sQuery(id+"F0.wireOp",EDGE,"E625"),sQuery(id+"F0.wireOp",EDGE,"E626"),sQuery(id+"F0.wireOp",EDGE,"E627"),sQuery(id+"F0.wireOp",EDGE,"E628")])],"isStart":false});
            var Q1;
            Q1=makeQuery(id+"F2.opExtrude","CAP_FACE",FACE,{"disambiguationData":[OSD([sQuery(id+"F0.wireOp",EDGE,"E184"),sQuery(id+"F0.wireOp",EDGE,"E185"),sQuery(id+"F0.wireOp",EDGE,"E186"),sQuery(id+"F0.wireOp",EDGE,"E187"),sQuery(id+"F0.wireOp",EDGE,"E188"),sQuery(id+"F0.wireOp",EDGE,"E189"),sQuery(id+"F0.wireOp",EDGE,"E190"),sQuery(id+"F0.wireOp",EDGE,"E191"),sQuery(id+"F0.wireOp",EDGE,"E192"),sQuery(id+"F0.wireOp",EDGE,"E193"),sQuery(id+"F0.wireOp",EDGE,"E194"),sQuery(id+"F0.wireOp",EDGE,"E195"),sQuery(id+"F0.wireOp",EDGE,"E196"),sQuery(id+"F0.wireOp",EDGE,"E197"),sQuery(id+"F0.wireOp",EDGE,"E198"),sQuery(id+"F0.wireOp",EDGE,"E199"),sQuery(id+"F0.wireOp",EDGE,"E200"),sQuery(id+"F0.wireOp",EDGE,"E201"),sQuery(id+"F0.wireOp",EDGE,"E202"),sQuery(id+"F0.wireOp",EDGE,"E203"),sQuery(id+"F0.wireOp",EDGE,"E204"),sQuery(id+"F0.wireOp",EDGE,"E205"),sQuery(id+"F0.wireOp",EDGE,"E206"),sQuery(id+"F0.wireOp",EDGE,"E207"),sQuery(id+"F0.wireOp",EDGE,"E208"),sQuery(id+"F0.wireOp",EDGE,"E209"),sQuery(id+"F0.wireOp",EDGE,"E210"),sQuery(id+"F0.wireOp",EDGE,"E211"),sQuery(id+"F0.wireOp",EDGE,"E212"),sQuery(id+"F0.wireOp",EDGE,"E213"),sQuery(id+"F0.wireOp",EDGE,"E214"),sQuery(id+"F0.wireOp",EDGE,"E215"),sQuery(id+"F0.wireOp",EDGE,"E216"),sQuery(id+"F0.wireOp",EDGE,"E217"),sQuery(id+"F0.wireOp",EDGE,"E218"),sQuery(id+"F0.wireOp",EDGE,"E219"),sQuery(id+"F0.wireOp",EDGE,"E220"),sQuery(id+"F0.wireOp",EDGE,"E221"),sQuery(id+"F0.wireOp",EDGE,"E222"),sQuery(id+"F0.wireOp",EDGE,"E223"),sQuery(id+"F0.wireOp",EDGE,"E224"),sQuery(id+"F0.wireOp",EDGE,"E225"),sQuery(id+"F0.wireOp",EDGE,"E226"),sQuery(id+"F0.wireOp",EDGE,"E227"),sQuery(id+"F0.wireOp",EDGE,"E228"),sQuery(id+"F0.wireOp",EDGE,"E229"),sQuery(id+"F0.wireOp",EDGE,"E230"),sQuery(id+"F0.wireOp",EDGE,"E231"),sQuery(id+"F0.wireOp",EDGE,"E232"),sQuery(id+"F0.wireOp",EDGE,"E233"),sQuery(id+"F0.wireOp",EDGE,"E234"),sQuery(id+"F0.wireOp",EDGE,"E235"),sQuery(id+"F0.wireOp",EDGE,"E236"),sQuery(id+"F0.wireOp",EDGE,"E237"),sQuery(id+"F0.wireOp",EDGE,"E238"),sQuery(id+"F0.wireOp",EDGE,"E239"),sQuery(id+"F0.wireOp",EDGE,"E240"),sQuery(id+"F0.wireOp",EDGE,"E241"),sQuery(id+"F0.wireOp",EDGE,"E242"),sQuery(id+"F0.wireOp",EDGE,"E243"),sQuery(id+"F0.wireOp",EDGE,"E244"),sQuery(id+"F0.wireOp",EDGE,"E245"),sQuery(id+"F0.wireOp",EDGE,"E246"),sQuery(id+"F0.wireOp",EDGE,"E247"),sQuery(id+"F0.wireOp",EDGE,"E248"),sQuery(id+"F0.wireOp",EDGE,"E249"),sQuery(id+"F0.wireOp",EDGE,"E250"),sQuery(id+"F0.wireOp",EDGE,"E251"),sQuery(id+"F0.wireOp",EDGE,"E252"),sQuery(id+"F0.wireOp",EDGE,"E253"),sQuery(id+"F0.wireOp",EDGE,"E254"),sQuery(id+"F0.wireOp",EDGE,"E255"),sQuery(id+"F0.wireOp",EDGE,"E256"),sQuery(id+"F0.wireOp",EDGE,"E257"),sQuery(id+"F0.wireOp",EDGE,"E258"),sQuery(id+"F0.wireOp",EDGE,"E259"),sQuery(id+"F0.wireOp",EDGE,"E260"),sQuery(id+"F0.wireOp",EDGE,"E261"),sQuery(id+"F0.wireOp",EDGE,"E262"),sQuery(id+"F0.wireOp",EDGE,"E263"),sQuery(id+"F0.wireOp",EDGE,"E264"),sQuery(id+"F0.wireOp",EDGE,"E265"),sQuery(id+"F0.wireOp",EDGE,"E266"),sQuery(id+"F0.wireOp",EDGE,"E267"),sQuery(id+"F0.wireOp",EDGE,"E268"),sQuery(id+"F0.wireOp",EDGE,"E269"),sQuery(id+"F0.wireOp",EDGE,"E270"),sQuery(id+"F0.wireOp",EDGE,"E271"),sQuery(id+"F0.wireOp",EDGE,"E272"),sQuery(id+"F0.wireOp",EDGE,"E273"),sQuery(id+"F0.wireOp",EDGE,"E274"),sQuery(id+"F0.wireOp",EDGE,"E275"),sQuery(id+"F0.wireOp",EDGE,"E276"),sQuery(id+"F0.wireOp",EDGE,"E277"),sQuery(id+"F0.wireOp",EDGE,"E278"),sQuery(id+"F0.wireOp",EDGE,"E279"),sQuery(id+"F0.wireOp",EDGE,"E280"),sQuery(id+"F0.wireOp",EDGE,"E281"),sQuery(id+"F0.wireOp",EDGE,"E282"),sQuery(id+"F0.wireOp",EDGE,"E283"),sQuery(id+"F0.wireOp",EDGE,"E284"),sQuery(id+"F0.wireOp",EDGE,"E285"),sQuery(id+"F0.wireOp",EDGE,"E286"),sQuery(id+"F0.wireOp",EDGE,"E287"),sQuery(id+"F0.wireOp",EDGE,"E288"),sQuery(id+"F0.wireOp",EDGE,"E289"),sQuery(id+"F0.wireOp",EDGE,"E290"),sQuery(id+"F0.wireOp",EDGE,"E291"),sQuery(id+"F0.wireOp",EDGE,"E292"),sQuery(id+"F0.wireOp",EDGE,"E293"),sQuery(id+"F0.wireOp",EDGE,"E294"),sQuery(id+"F0.wireOp",EDGE,"E295"),sQuery(id+"F0.wireOp",EDGE,"E296"),sQuery(id+"F0.wireOp",EDGE,"E297"),sQuery(id+"F0.wireOp",EDGE,"E298"),sQuery(id+"F0.wireOp",EDGE,"E299"),sQuery(id+"F0.wireOp",EDGE,"E300"),sQuery(id+"F0.wireOp",EDGE,"E301"),sQuery(id+"F0.wireOp",EDGE,"E302"),sQuery(id+"F0.wireOp",EDGE,"E303"),sQuery(id+"F0.wireOp",EDGE,"E304"),sQuery(id+"F0.wireOp",EDGE,"E305"),sQuery(id+"F0.wireOp",EDGE,"E306"),sQuery(id+"F0.wireOp",EDGE,"E307"),sQuery(id+"F0.wireOp",EDGE,"E308"),sQuery(id+"F0.wireOp",EDGE,"E309"),sQuery(id+"F0.wireOp",EDGE,"E310"),sQuery(id+"F0.wireOp",EDGE,"E311"),sQuery(id+"F0.wireOp",EDGE,"E312"),sQuery(id+"F0.wireOp",EDGE,"E313"),sQuery(id+"F0.wireOp",EDGE,"E314"),sQuery(id+"F0.wireOp",EDGE,"E315"),sQuery(id+"F0.wireOp",EDGE,"E316"),sQuery(id+"F0.wireOp",EDGE,"E317"),sQuery(id+"F0.wireOp",EDGE,"E318"),sQuery(id+"F0.wireOp",EDGE,"E319"),sQuery(id+"F0.wireOp",EDGE,"E320"),sQuery(id+"F0.wireOp",EDGE,"E321"),sQuery(id+"F0.wireOp",EDGE,"E322"),sQuery(id+"F0.wireOp",EDGE,"E323"),sQuery(id+"F0.wireOp",EDGE,"E324"),sQuery(id+"F0.wireOp",EDGE,"E325"),sQuery(id+"F0.wireOp",EDGE,"E326"),sQuery(id+"F0.wireOp",EDGE,"E327"),sQuery(id+"F0.wireOp",EDGE,"E328"),sQuery(id+"F0.wireOp",EDGE,"E329"),sQuery(id+"F0.wireOp",EDGE,"E330"),sQuery(id+"F0.wireOp",EDGE,"E331"),sQuery(id+"F0.wireOp",EDGE,"E332"),sQuery(id+"F0.wireOp",EDGE,"E333"),sQuery(id+"F0.wireOp",EDGE,"E334"),sQuery(id+"F0.wireOp",EDGE,"E335"),sQuery(id+"F0.wireOp",EDGE,"E336"),sQuery(id+"F0.wireOp",EDGE,"E337"),sQuery(id+"F0.wireOp",EDGE,"E338"),sQuery(id+"F0.wireOp",EDGE,"E339"),sQuery(id+"F0.wireOp",EDGE,"E340"),sQuery(id+"F0.wireOp",EDGE,"E341"),sQuery(id+"F0.wireOp",EDGE,"E342"),sQuery(id+"F0.wireOp",EDGE,"E343"),sQuery(id+"F0.wireOp",EDGE,"E344"),sQuery(id+"F0.wireOp",EDGE,"E345"),sQuery(id+"F0.wireOp",EDGE,"E346"),sQuery(id+"F0.wireOp",EDGE,"E347"),sQuery(id+"F0.wireOp",EDGE,"E348"),sQuery(id+"F0.wireOp",EDGE,"E349"),sQuery(id+"F0.wireOp",EDGE,"E350"),sQuery(id+"F0.wireOp",EDGE,"E351"),sQuery(id+"F0.wireOp",EDGE,"E352"),sQuery(id+"F0.wireOp",EDGE,"E353"),sQuery(id+"F0.wireOp",EDGE,"E354"),sQuery(id+"F0.wireOp",EDGE,"E355"),sQuery(id+"F0.wireOp",EDGE,"E356")])],"isStart":false});
            var Q2;
            Q2=makeQuery(id+"F2.opExtrude","CAP_FACE",FACE,{"disambiguationData":[OSD([sQuery(id+"F0.wireOp",EDGE,"E629"),sQuery(id+"F0.wireOp",EDGE,"E630"),sQuery(id+"F0.wireOp",EDGE,"E631"),sQuery(id+"F0.wireOp",EDGE,"E632"),sQuery(id+"F0.wireOp",EDGE,"E633"),sQuery(id+"F0.wireOp",EDGE,"E634"),sQuery(id+"F0.wireOp",EDGE,"E635"),sQuery(id+"F0.wireOp",EDGE,"E636"),sQuery(id+"F0.wireOp",EDGE,"E637"),sQuery(id+"F0.wireOp",EDGE,"E638"),sQuery(id+"F0.wireOp",EDGE,"E639"),sQuery(id+"F0.wireOp",EDGE,"E640"),sQuery(id+"F0.wireOp",EDGE,"E641"),sQuery(id+"F0.wireOp",EDGE,"E642"),sQuery(id+"F0.wireOp",EDGE,"E643"),sQuery(id+"F0.wireOp",EDGE,"E644"),sQuery(id+"F0.wireOp",EDGE,"E645"),sQuery(id+"F0.wireOp",EDGE,"E646"),sQuery(id+"F0.wireOp",EDGE,"E647"),sQuery(id+"F0.wireOp",EDGE,"E648"),sQuery(id+"F0.wireOp",EDGE,"E649"),sQuery(id+"F0.wireOp",EDGE,"E650"),sQuery(id+"F0.wireOp",EDGE,"E651"),sQuery(id+"F0.wireOp",EDGE,"E652"),sQuery(id+"F0.wireOp",EDGE,"E653"),sQuery(id+"F0.wireOp",EDGE,"E654"),sQuery(id+"F0.wireOp",EDGE,"E655"),sQuery(id+"F0.wireOp",EDGE,"E656"),sQuery(id+"F0.wireOp",EDGE,"E657"),sQuery(id+"F0.wireOp",EDGE,"E658"),sQuery(id+"F0.wireOp",EDGE,"E659"),sQuery(id+"F0.wireOp",EDGE,"E660"),sQuery(id+"F0.wireOp",EDGE,"E661"),sQuery(id+"F0.wireOp",EDGE,"E662"),sQuery(id+"F0.wireOp",EDGE,"E663"),sQuery(id+"F0.wireOp",EDGE,"E664"),sQuery(id+"F0.wireOp",EDGE,"E665"),sQuery(id+"F0.wireOp",EDGE,"E666"),sQuery(id+"F0.wireOp",EDGE,"E667"),sQuery(id+"F0.wireOp",EDGE,"E668"),sQuery(id+"F0.wireOp",EDGE,"E669"),sQuery(id+"F0.wireOp",EDGE,"E670"),sQuery(id+"F0.wireOp",EDGE,"E671"),sQuery(id+"F0.wireOp",EDGE,"E672"),sQuery(id+"F0.wireOp",EDGE,"E673"),sQuery(id+"F0.wireOp",EDGE,"E674"),sQuery(id+"F0.wireOp",EDGE,"E675"),sQuery(id+"F0.wireOp",EDGE,"E676"),sQuery(id+"F0.wireOp",EDGE,"E677"),sQuery(id+"F0.wireOp",EDGE,"E678"),sQuery(id+"F0.wireOp",EDGE,"E679"),sQuery(id+"F0.wireOp",EDGE,"E680"),sQuery(id+"F0.wireOp",EDGE,"E681"),sQuery(id+"F0.wireOp",EDGE,"E682"),sQuery(id+"F0.wireOp",EDGE,"E683"),sQuery(id+"F0.wireOp",EDGE,"E684"),sQuery(id+"F0.wireOp",EDGE,"E685"),sQuery(id+"F0.wireOp",EDGE,"E686"),sQuery(id+"F0.wireOp",EDGE,"E687"),sQuery(id+"F0.wireOp",EDGE,"E688"),sQuery(id+"F0.wireOp",EDGE,"E689"),sQuery(id+"F0.wireOp",EDGE,"E690"),sQuery(id+"F0.wireOp",EDGE,"E691"),sQuery(id+"F0.wireOp",EDGE,"E692"),sQuery(id+"F0.wireOp",EDGE,"E693"),sQuery(id+"F0.wireOp",EDGE,"E694"),sQuery(id+"F0.wireOp",EDGE,"E695"),sQuery(id+"F0.wireOp",EDGE,"E696"),sQuery(id+"F0.wireOp",EDGE,"E697"),sQuery(id+"F0.wireOp",EDGE,"E698"),sQuery(id+"F0.wireOp",EDGE,"E699"),sQuery(id+"F0.wireOp",EDGE,"E700"),sQuery(id+"F0.wireOp",EDGE,"E701"),sQuery(id+"F0.wireOp",EDGE,"E702"),sQuery(id+"F0.wireOp",EDGE,"E703"),sQuery(id+"F0.wireOp",EDGE,"E704"),sQuery(id+"F0.wireOp",EDGE,"E705"),sQuery(id+"F0.wireOp",EDGE,"E706"),sQuery(id+"F0.wireOp",EDGE,"E707"),sQuery(id+"F0.wireOp",EDGE,"E708"),sQuery(id+"F0.wireOp",EDGE,"E709"),sQuery(id+"F0.wireOp",EDGE,"E710"),sQuery(id+"F0.wireOp",EDGE,"E711"),sQuery(id+"F0.wireOp",EDGE,"E712"),sQuery(id+"F0.wireOp",EDGE,"E713"),sQuery(id+"F0.wireOp",EDGE,"E714")])],"isStart":false});
            var Q3;
            Q3=makeQuery(id+"F2.opExtrude","CAP_FACE",FACE,{"disambiguationData":[OSD([sQuery(id+"F0.wireOp",EDGE,"E48"),sQuery(id+"F0.wireOp",EDGE,"E49"),sQuery(id+"F0.wireOp",EDGE,"E50"),sQuery(id+"F0.wireOp",EDGE,"E51"),sQuery(id+"F0.wireOp",EDGE,"E52"),sQuery(id+"F0.wireOp",EDGE,"E53"),sQuery(id+"F0.wireOp",EDGE,"E54"),sQuery(id+"F0.wireOp",EDGE,"E55"),sQuery(id+"F0.wireOp",EDGE,"E56"),sQuery(id+"F0.wireOp",EDGE,"E57"),sQuery(id+"F0.wireOp",EDGE,"E58"),sQuery(id+"F0.wireOp",EDGE,"E59"),sQuery(id+"F0.wireOp",EDGE,"E60"),sQuery(id+"F0.wireOp",EDGE,"E61"),sQuery(id+"F0.wireOp",EDGE,"E62"),sQuery(id+"F0.wireOp",EDGE,"E63"),sQuery(id+"F0.wireOp",EDGE,"E64"),sQuery(id+"F0.wireOp",EDGE,"E65"),sQuery(id+"F0.wireOp",EDGE,"E66"),sQuery(id+"F0.wireOp",EDGE,"E67"),sQuery(id+"F0.wireOp",EDGE,"E68"),sQuery(id+"F0.wireOp",EDGE,"E69"),sQuery(id+"F0.wireOp",EDGE,"E70"),sQuery(id+"F0.wireOp",EDGE,"E71"),sQuery(id+"F0.wireOp",EDGE,"E72"),sQuery(id+"F0.wireOp",EDGE,"E73"),sQuery(id+"F0.wireOp",EDGE,"E74"),sQuery(id+"F0.wireOp",EDGE,"E75"),sQuery(id+"F0.wireOp",EDGE,"E76"),sQuery(id+"F0.wireOp",EDGE,"E77"),sQuery(id+"F0.wireOp",EDGE,"E78"),sQuery(id+"F0.wireOp",EDGE,"E79"),sQuery(id+"F0.wireOp",EDGE,"E80"),sQuery(id+"F0.wireOp",EDGE,"E81"),sQuery(id+"F0.wireOp",EDGE,"E82"),sQuery(id+"F0.wireOp",EDGE,"E83"),sQuery(id+"F0.wireOp",EDGE,"E84"),sQuery(id+"F0.wireOp",EDGE,"E85"),sQuery(id+"F0.wireOp",EDGE,"E86"),sQuery(id+"F0.wireOp",EDGE,"E87"),sQuery(id+"F0.wireOp",EDGE,"E88"),sQuery(id+"F0.wireOp",EDGE,"E89"),sQuery(id+"F0.wireOp",EDGE,"E90"),sQuery(id+"F0.wireOp",EDGE,"E91"),sQuery(id+"F0.wireOp",EDGE,"E92"),sQuery(id+"F0.wireOp",EDGE,"E93"),sQuery(id+"F0.wireOp",EDGE,"E94"),sQuery(id+"F0.wireOp",EDGE,"E95"),sQuery(id+"F0.wireOp",EDGE,"E96"),sQuery(id+"F0.wireOp",EDGE,"E97"),sQuery(id+"F0.wireOp",EDGE,"E98"),sQuery(id+"F0.wireOp",EDGE,"E99"),sQuery(id+"F0.wireOp",EDGE,"E100"),sQuery(id+"F0.wireOp",EDGE,"E101"),sQuery(id+"F0.wireOp",EDGE,"E102"),sQuery(id+"F0.wireOp",EDGE,"E103"),sQuery(id+"F0.wireOp",EDGE,"E104"),sQuery(id+"F0.wireOp",EDGE,"E105"),sQuery(id+"F0.wireOp",EDGE,"E106"),sQuery(id+"F0.wireOp",EDGE,"E107"),sQuery(id+"F0.wireOp",EDGE,"E108"),sQuery(id+"F0.wireOp",EDGE,"E109"),sQuery(id+"F0.wireOp",EDGE,"E110"),sQuery(id+"F0.wireOp",EDGE,"E111"),sQuery(id+"F0.wireOp",EDGE,"E112"),sQuery(id+"F0.wireOp",EDGE,"E113"),sQuery(id+"F0.wireOp",EDGE,"E114"),sQuery(id+"F0.wireOp",EDGE,"E115"),sQuery(id+"F0.wireOp",EDGE,"E116"),sQuery(id+"F0.wireOp",EDGE,"E117"),sQuery(id+"F0.wireOp",EDGE,"E118"),sQuery(id+"F0.wireOp",EDGE,"E119"),sQuery(id+"F0.wireOp",EDGE,"E120"),sQuery(id+"F0.wireOp",EDGE,"E121"),sQuery(id+"F0.wireOp",EDGE,"E122"),sQuery(id+"F0.wireOp",EDGE,"E123"),sQuery(id+"F0.wireOp",EDGE,"E124"),sQuery(id+"F0.wireOp",EDGE,"E125"),sQuery(id+"F0.wireOp",EDGE,"E126"),sQuery(id+"F0.wireOp",EDGE,"E127"),sQuery(id+"F0.wireOp",EDGE,"E128"),sQuery(id+"F0.wireOp",EDGE,"E129"),sQuery(id+"F0.wireOp",EDGE,"E130"),sQuery(id+"F0.wireOp",EDGE,"E131"),sQuery(id+"F0.wireOp",EDGE,"E132"),sQuery(id+"F0.wireOp",EDGE,"E133"),sQuery(id+"F0.wireOp",EDGE,"E134"),sQuery(id+"F0.wireOp",EDGE,"E135"),sQuery(id+"F0.wireOp",EDGE,"E136"),sQuery(id+"F0.wireOp",EDGE,"E137"),sQuery(id+"F0.wireOp",EDGE,"E138"),sQuery(id+"F0.wireOp",EDGE,"E139"),sQuery(id+"F0.wireOp",EDGE,"E140"),sQuery(id+"F0.wireOp",EDGE,"E141"),sQuery(id+"F0.wireOp",EDGE,"E142"),sQuery(id+"F0.wireOp",EDGE,"E143"),sQuery(id+"F0.wireOp",EDGE,"E144"),sQuery(id+"F0.wireOp",EDGE,"E145"),sQuery(id+"F0.wireOp",EDGE,"E146"),sQuery(id+"F0.wireOp",EDGE,"E147"),sQuery(id+"F0.wireOp",EDGE,"E148"),sQuery(id+"F0.wireOp",EDGE,"E149"),sQuery(id+"F0.wireOp",EDGE,"E150"),sQuery(id+"F0.wireOp",EDGE,"E151"),sQuery(id+"F0.wireOp",EDGE,"E152"),sQuery(id+"F0.wireOp",EDGE,"E153"),sQuery(id+"F0.wireOp",EDGE,"E154"),sQuery(id+"F0.wireOp",EDGE,"E155"),sQuery(id+"F0.wireOp",EDGE,"E156"),sQuery(id+"F0.wireOp",EDGE,"E157"),sQuery(id+"F0.wireOp",EDGE,"E158"),sQuery(id+"F0.wireOp",EDGE,"E159"),sQuery(id+"F0.wireOp",EDGE,"E160"),sQuery(id+"F0.wireOp",EDGE,"E161"),sQuery(id+"F0.wireOp",EDGE,"E162"),sQuery(id+"F0.wireOp",EDGE,"E163"),sQuery(id+"F0.wireOp",EDGE,"E164"),sQuery(id+"F0.wireOp",EDGE,"E165"),sQuery(id+"F0.wireOp",EDGE,"E166"),sQuery(id+"F0.wireOp",EDGE,"E167"),sQuery(id+"F0.wireOp",EDGE,"E168"),sQuery(id+"F0.wireOp",EDGE,"E169"),sQuery(id+"F0.wireOp",EDGE,"E170"),sQuery(id+"F0.wireOp",EDGE,"E171"),sQuery(id+"F0.wireOp",EDGE,"E172"),sQuery(id+"F0.wireOp",EDGE,"E173"),sQuery(id+"F0.wireOp",EDGE,"E174"),sQuery(id+"F0.wireOp",EDGE,"E175"),sQuery(id+"F0.wireOp",EDGE,"E176"),sQuery(id+"F0.wireOp",EDGE,"E177"),sQuery(id+"F0.wireOp",EDGE,"E178"),sQuery(id+"F0.wireOp",EDGE,"E179"),sQuery(id+"F0.wireOp",EDGE,"E180"),sQuery(id+"F0.wireOp",EDGE,"E181"),sQuery(id+"F0.wireOp",EDGE,"E182"),sQuery(id+"F0.wireOp",EDGE,"E183")])],"isStart":false});
            shell(context, id + "F3", {"entities" : qUnion([Q0, Q1, Q2, Q3]), "thickness" : 2.54 * mm, "oppositeDirection" : true});
        }
        {
            var Q0;
            Q0=makeQuery(id+"F2.opExtrude","CAP_FACE",FACE,{"disambiguationData":[OSD([sQuery(id+"F0.wireOp",EDGE,"E357"),sQuery(id+"F0.wireOp",EDGE,"E358"),sQuery(id+"F0.wireOp",EDGE,"E359"),sQuery(id+"F0.wireOp",EDGE,"E360"),sQuery(id+"F0.wireOp",EDGE,"E361"),sQuery(id+"F0.wireOp",EDGE,"E362"),sQuery(id+"F0.wireOp",EDGE,"E363"),sQuery(id+"F0.wireOp",EDGE,"E364"),sQuery(id+"F0.wireOp",EDGE,"E365"),sQuery(id+"F0.wireOp",EDGE,"E366"),sQuery(id+"F0.wireOp",EDGE,"E367"),sQuery(id+"F0.wireOp",EDGE,"E368"),sQuery(id+"F0.wireOp",EDGE,"E369"),sQuery(id+"F0.wireOp",EDGE,"E370"),sQuery(id+"F0.wireOp",EDGE,"E371"),sQuery(id+"F0.wireOp",EDGE,"E372"),sQuery(id+"F0.wireOp",EDGE,"E373"),sQuery(id+"F0.wireOp",EDGE,"E374"),sQuery(id+"F0.wireOp",EDGE,"E375"),sQuery(id+"F0.wireOp",EDGE,"E376"),sQuery(id+"F0.wireOp",EDGE,"E377"),sQuery(id+"F0.wireOp",EDGE,"E378"),sQuery(id+"F0.wireOp",EDGE,"E379"),sQuery(id+"F0.wireOp",EDGE,"E380"),sQuery(id+"F0.wireOp",EDGE,"E381"),sQuery(id+"F0.wireOp",EDGE,"E382"),sQuery(id+"F0.wireOp",EDGE,"E383"),sQuery(id+"F0.wireOp",EDGE,"E384"),sQuery(id+"F0.wireOp",EDGE,"E385"),sQuery(id+"F0.wireOp",EDGE,"E386"),sQuery(id+"F0.wireOp",EDGE,"E387"),sQuery(id+"F0.wireOp",EDGE,"E388"),sQuery(id+"F0.wireOp",EDGE,"E389"),sQuery(id+"F0.wireOp",EDGE,"E390"),sQuery(id+"F0.wireOp",EDGE,"E391"),sQuery(id+"F0.wireOp",EDGE,"E392"),sQuery(id+"F0.wireOp",EDGE,"E393"),sQuery(id+"F0.wireOp",EDGE,"E394"),sQuery(id+"F0.wireOp",EDGE,"E395"),sQuery(id+"F0.wireOp",EDGE,"E396"),sQuery(id+"F0.wireOp",EDGE,"E397"),sQuery(id+"F0.wireOp",EDGE,"E398"),sQuery(id+"F0.wireOp",EDGE,"E399"),sQuery(id+"F0.wireOp",EDGE,"E400"),sQuery(id+"F0.wireOp",EDGE,"E401"),sQuery(id+"F0.wireOp",EDGE,"E402"),sQuery(id+"F0.wireOp",EDGE,"E403"),sQuery(id+"F0.wireOp",EDGE,"E404"),sQuery(id+"F0.wireOp",EDGE,"E405"),sQuery(id+"F0.wireOp",EDGE,"E406"),sQuery(id+"F0.wireOp",EDGE,"E407"),sQuery(id+"F0.wireOp",EDGE,"E408"),sQuery(id+"F0.wireOp",EDGE,"E409"),sQuery(id+"F0.wireOp",EDGE,"E410"),sQuery(id+"F0.wireOp",EDGE,"E411"),sQuery(id+"F0.wireOp",EDGE,"E412"),sQuery(id+"F0.wireOp",EDGE,"E413"),sQuery(id+"F0.wireOp",EDGE,"E414"),sQuery(id+"F0.wireOp",EDGE,"E415"),sQuery(id+"F0.wireOp",EDGE,"E416"),sQuery(id+"F0.wireOp",EDGE,"E417"),sQuery(id+"F0.wireOp",EDGE,"E418"),sQuery(id+"F0.wireOp",EDGE,"E419"),sQuery(id+"F0.wireOp",EDGE,"E420"),sQuery(id+"F0.wireOp",EDGE,"E421"),sQuery(id+"F0.wireOp",EDGE,"E422"),sQuery(id+"F0.wireOp",EDGE,"E423"),sQuery(id+"F0.wireOp",EDGE,"E424"),sQuery(id+"F0.wireOp",EDGE,"E425"),sQuery(id+"F0.wireOp",EDGE,"E426"),sQuery(id+"F0.wireOp",EDGE,"E427"),sQuery(id+"F0.wireOp",EDGE,"E428"),sQuery(id+"F0.wireOp",EDGE,"E429"),sQuery(id+"F0.wireOp",EDGE,"E430"),sQuery(id+"F0.wireOp",EDGE,"E431"),sQuery(id+"F0.wireOp",EDGE,"E432"),sQuery(id+"F0.wireOp",EDGE,"E433"),sQuery(id+"F0.wireOp",EDGE,"E434"),sQuery(id+"F0.wireOp",EDGE,"E435"),sQuery(id+"F0.wireOp",EDGE,"E436"),sQuery(id+"F0.wireOp",EDGE,"E437"),sQuery(id+"F0.wireOp",EDGE,"E438"),sQuery(id+"F0.wireOp",EDGE,"E439"),sQuery(id+"F0.wireOp",EDGE,"E440"),sQuery(id+"F0.wireOp",EDGE,"E441"),sQuery(id+"F0.wireOp",EDGE,"E442"),sQuery(id+"F0.wireOp",EDGE,"E443"),sQuery(id+"F0.wireOp",EDGE,"E444"),sQuery(id+"F0.wireOp",EDGE,"E445"),sQuery(id+"F0.wireOp",EDGE,"E446"),sQuery(id+"F0.wireOp",EDGE,"E447"),sQuery(id+"F0.wireOp",EDGE,"E448"),sQuery(id+"F0.wireOp",EDGE,"E449"),sQuery(id+"F0.wireOp",EDGE,"E450"),sQuery(id+"F0.wireOp",EDGE,"E451"),sQuery(id+"F0.wireOp",EDGE,"E452"),sQuery(id+"F0.wireOp",EDGE,"E453"),sQuery(id+"F0.wireOp",EDGE,"E454"),sQuery(id+"F0.wireOp",EDGE,"E455"),sQuery(id+"F0.wireOp",EDGE,"E456"),sQuery(id+"F0.wireOp",EDGE,"E457"),sQuery(id+"F0.wireOp",EDGE,"E458"),sQuery(id+"F0.wireOp",EDGE,"E459"),sQuery(id+"F0.wireOp",EDGE,"E460"),sQuery(id+"F0.wireOp",EDGE,"E461"),sQuery(id+"F0.wireOp",EDGE,"E462"),sQuery(id+"F0.wireOp",EDGE,"E463"),sQuery(id+"F0.wireOp",EDGE,"E464"),sQuery(id+"F0.wireOp",EDGE,"E465"),sQuery(id+"F0.wireOp",EDGE,"E466"),sQuery(id+"F0.wireOp",EDGE,"E467"),sQuery(id+"F0.wireOp",EDGE,"E468"),sQuery(id+"F0.wireOp",EDGE,"E469"),sQuery(id+"F0.wireOp",EDGE,"E470"),sQuery(id+"F0.wireOp",EDGE,"E471"),sQuery(id+"F0.wireOp",EDGE,"E472"),sQuery(id+"F0.wireOp",EDGE,"E473"),sQuery(id+"F0.wireOp",EDGE,"E474"),sQuery(id+"F0.wireOp",EDGE,"E475"),sQuery(id+"F0.wireOp",EDGE,"E476"),sQuery(id+"F0.wireOp",EDGE,"E477"),sQuery(id+"F0.wireOp",EDGE,"E478"),sQuery(id+"F0.wireOp",EDGE,"E479"),sQuery(id+"F0.wireOp",EDGE,"E480"),sQuery(id+"F0.wireOp",EDGE,"E481"),sQuery(id+"F0.wireOp",EDGE,"E482"),sQuery(id+"F0.wireOp",EDGE,"E483"),sQuery(id+"F0.wireOp",EDGE,"E484"),sQuery(id+"F0.wireOp",EDGE,"E485"),sQuery(id+"F0.wireOp",EDGE,"E486"),sQuery(id+"F0.wireOp",EDGE,"E487"),sQuery(id+"F0.wireOp",EDGE,"E488"),sQuery(id+"F0.wireOp",EDGE,"E489"),sQuery(id+"F0.wireOp",EDGE,"E490"),sQuery(id+"F0.wireOp",EDGE,"E491"),sQuery(id+"F0.wireOp",EDGE,"E492"),sQuery(id+"F0.wireOp",EDGE,"E493"),sQuery(id+"F0.wireOp",EDGE,"E494"),sQuery(id+"F0.wireOp",EDGE,"E495"),sQuery(id+"F0.wireOp",EDGE,"E496"),sQuery(id+"F0.wireOp",EDGE,"E497"),sQuery(id+"F0.wireOp",EDGE,"E498"),sQuery(id+"F0.wireOp",EDGE,"E499"),sQuery(id+"F0.wireOp",EDGE,"E500"),sQuery(id+"F0.wireOp",EDGE,"E501"),sQuery(id+"F0.wireOp",EDGE,"E502"),sQuery(id+"F0.wireOp",EDGE,"E503"),sQuery(id+"F0.wireOp",EDGE,"E504"),sQuery(id+"F0.wireOp",EDGE,"E505"),sQuery(id+"F0.wireOp",EDGE,"E506"),sQuery(id+"F0.wireOp",EDGE,"E507"),sQuery(id+"F0.wireOp",EDGE,"E508"),sQuery(id+"F0.wireOp",EDGE,"E509"),sQuery(id+"F0.wireOp",EDGE,"E510"),sQuery(id+"F0.wireOp",EDGE,"E511"),sQuery(id+"F0.wireOp",EDGE,"E512"),sQuery(id+"F0.wireOp",EDGE,"E513"),sQuery(id+"F0.wireOp",EDGE,"E514"),sQuery(id+"F0.wireOp",EDGE,"E515"),sQuery(id+"F0.wireOp",EDGE,"E516"),sQuery(id+"F0.wireOp",EDGE,"E517"),sQuery(id+"F0.wireOp",EDGE,"E518"),sQuery(id+"F0.wireOp",EDGE,"E519"),sQuery(id+"F0.wireOp",EDGE,"E520"),sQuery(id+"F0.wireOp",EDGE,"E521"),sQuery(id+"F0.wireOp",EDGE,"E522"),sQuery(id+"F0.wireOp",EDGE,"E523"),sQuery(id+"F0.wireOp",EDGE,"E524"),sQuery(id+"F0.wireOp",EDGE,"E525"),sQuery(id+"F0.wireOp",EDGE,"E526"),sQuery(id+"F0.wireOp",EDGE,"E527"),sQuery(id+"F0.wireOp",EDGE,"E528"),sQuery(id+"F0.wireOp",EDGE,"E529"),sQuery(id+"F0.wireOp",EDGE,"E530"),sQuery(id+"F0.wireOp",EDGE,"E531"),sQuery(id+"F0.wireOp",EDGE,"E532"),sQuery(id+"F0.wireOp",EDGE,"E533"),sQuery(id+"F0.wireOp",EDGE,"E534"),sQuery(id+"F0.wireOp",EDGE,"E535"),sQuery(id+"F0.wireOp",EDGE,"E536"),sQuery(id+"F0.wireOp",EDGE,"E537"),sQuery(id+"F0.wireOp",EDGE,"E538"),sQuery(id+"F0.wireOp",EDGE,"E539"),sQuery(id+"F0.wireOp",EDGE,"E540"),sQuery(id+"F0.wireOp",EDGE,"E541"),sQuery(id+"F0.wireOp",EDGE,"E542"),sQuery(id+"F0.wireOp",EDGE,"E543"),sQuery(id+"F0.wireOp",EDGE,"E544"),sQuery(id+"F0.wireOp",EDGE,"E545"),sQuery(id+"F0.wireOp",EDGE,"E546"),sQuery(id+"F0.wireOp",EDGE,"E547"),sQuery(id+"F0.wireOp",EDGE,"E548"),sQuery(id+"F0.wireOp",EDGE,"E549"),sQuery(id+"F0.wireOp",EDGE,"E550"),sQuery(id+"F0.wireOp",EDGE,"E551"),sQuery(id+"F0.wireOp",EDGE,"E552"),sQuery(id+"F0.wireOp",EDGE,"E553"),sQuery(id+"F0.wireOp",EDGE,"E554"),sQuery(id+"F0.wireOp",EDGE,"E555"),sQuery(id+"F0.wireOp",EDGE,"E556"),sQuery(id+"F0.wireOp",EDGE,"E557"),sQuery(id+"F0.wireOp",EDGE,"E558"),sQuery(id+"F0.wireOp",EDGE,"E559"),sQuery(id+"F0.wireOp",EDGE,"E560"),sQuery(id+"F0.wireOp",EDGE,"E561"),sQuery(id+"F0.wireOp",EDGE,"E562"),sQuery(id+"F0.wireOp",EDGE,"E563"),sQuery(id+"F0.wireOp",EDGE,"E564"),sQuery(id+"F0.wireOp",EDGE,"E565"),sQuery(id+"F0.wireOp",EDGE,"E566"),sQuery(id+"F0.wireOp",EDGE,"E567"),sQuery(id+"F0.wireOp",EDGE,"E568")])],"isStart":false});
            shell(context, id + "F4", {"entities" : qUnion([Q0]), "thickness" : 2.54 * mm});
        }
        {
            var Q0;
            Q0=makeQuery(id+"F0.imprint","IMPRINT",FACE,{"disambiguationData":[TD([[makeQuery(id+"F0.imprint","IMPRINT",EDGE,{"derivedFrom":sQuery(id+"F0.wireOp",EDGE,"E184")}),1.0]])]});
            var Q1;
            Q1=makeQuery(id+"F0.imprint","IMPRINT",FACE,{"disambiguationData":[TD([[makeQuery(id+"F0.imprint","IMPRINT",EDGE,{"derivedFrom":sQuery(id+"F0.wireOp",EDGE,"E569")}),1.0]])]});
            var Q2;
            Q2=makeQuery(id+"F0.imprint","IMPRINT",FACE,{"disambiguationData":[TD([[makeQuery(id+"F0.imprint","IMPRINT",EDGE,{"derivedFrom":sQuery(id+"F0.wireOp",EDGE,"E629")}),1.0]])]});
            var Q3;
            Q3=makeQuery(id+"F0.imprint","IMPRINT",FACE,{"disambiguationData":[TD([[makeQuery(id+"F0.imprint","IMPRINT",EDGE,{"derivedFrom":sQuery(id+"F0.wireOp",EDGE,"E48")}),1.0]])]});
            var Q4;
            Q4=makeQuery(id+"F0.imprint","IMPRINT",FACE,{"disambiguationData":[TD([[makeQuery(id+"F0.imprint","IMPRINT",EDGE,{"derivedFrom":sQuery(id+"F0.wireOp",EDGE,"E357")}),1.0]])]});
            extrude(context, id + "F5", {"entities" : qUnion([Q0, Q1, Q2, Q3, Q4]), "depth" : 76.2 * mm, "offsetDistance" : 25.4 * mm});
        }
        {
            var Q0;
            Q0=makeQuery(id+"F1.opExtrude","CAP_FACE",FACE,{"disambiguationData":[OSD([sQuery(id+"F0.wireOp",EDGE,"E0"),sQuery(id+"F0.wireOp",EDGE,"E1"),sQuery(id+"F0.wireOp",EDGE,"E2"),sQuery(id+"F0.wireOp",EDGE,"E3"),sQuery(id+"F0.wireOp",EDGE,"E4"),sQuery(id+"F0.wireOp",EDGE,"E5"),sQuery(id+"F0.wireOp",EDGE,"E6"),sQuery(id+"F0.wireOp",EDGE,"E7"),sQuery(id+"F0.wireOp",EDGE,"E8"),sQuery(id+"F0.wireOp",EDGE,"E9"),sQuery(id+"F0.wireOp",EDGE,"E10"),sQuery(id+"F0.wireOp",EDGE,"E11"),sQuery(id+"F0.wireOp",EDGE,"E12"),sQuery(id+"F0.wireOp",EDGE,"E13"),sQuery(id+"F0.wireOp",EDGE,"E14"),sQuery(id+"F0.wireOp",EDGE,"E15"),sQuery(id+"F0.wireOp",EDGE,"E16"),sQuery(id+"F0.wireOp",EDGE,"E17"),sQuery(id+"F0.wireOp",EDGE,"E18"),sQuery(id+"F0.wireOp",EDGE,"E19"),sQuery(id+"F0.wireOp",EDGE,"E20"),sQuery(id+"F0.wireOp",EDGE,"E21"),sQuery(id+"F0.wireOp",EDGE,"E22"),sQuery(id+"F0.wireOp",EDGE,"E23"),sQuery(id+"F0.wireOp",EDGE,"E24"),sQuery(id+"F0.wireOp",EDGE,"E25"),sQuery(id+"F0.wireOp",EDGE,"E26"),sQuery(id+"F0.wireOp",EDGE,"E27"),sQuery(id+"F0.wireOp",EDGE,"E28"),sQuery(id+"F0.wireOp",EDGE,"E29"),sQuery(id+"F0.wireOp",EDGE,"E30"),sQuery(id+"F0.wireOp",EDGE,"E31"),sQuery(id+"F0.wireOp",EDGE,"E32"),sQuery(id+"F0.wireOp",EDGE,"E33"),sQuery(id+"F0.wireOp",EDGE,"E34"),sQuery(id+"F0.wireOp",EDGE,"E35"),sQuery(id+"F0.wireOp",EDGE,"E36"),sQuery(id+"F0.wireOp",EDGE,"E37"),sQuery(id+"F0.wireOp",EDGE,"E38"),sQuery(id+"F0.wireOp",EDGE,"E39"),sQuery(id+"F0.wireOp",EDGE,"E40"),sQuery(id+"F0.wireOp",EDGE,"E41"),sQuery(id+"F0.wireOp",EDGE,"E42"),sQuery(id+"F0.wireOp",EDGE,"E43")])],"isStart":true});
            var sketch = newSketch(context, id + "F6", { "sketchPlane" : qUnion([Q0])});
            skLineSegment(sketch, "E715.bottom", {"start": v(-713.1, 155.4) * mm, "end": v(-709.93, 155.4) * mm});
            skLineSegment(sketch, "E715.top", {"start": v(-713.1, -155.4) * mm, "end": v(-709.93, -155.4) * mm});
            skLineSegment(sketch, "E715.left", {"start": v(-713.1, 155.4) * mm, "end": v(-713.1, -155.4) * mm});
            skLineSegment(sketch, "E715.right", {"start": v(-709.93, 155.4) * mm, "end": v(-709.93, -155.4) * mm});
            skLineSegment(sketch, "E716.bottom", {"start": v(713.1, -155.4) * mm, "end": v(709.93, -155.4) * mm});
            skLineSegment(sketch, "E716.top", {"start": v(713.1, 155.4) * mm, "end": v(709.93, 155.4) * mm});
            skLineSegment(sketch, "E716.left", {"start": v(713.1, -155.4) * mm, "end": v(713.1, 155.4) * mm});
            skLineSegment(sketch, "E716.right", {"start": v(709.93, -155.4) * mm, "end": v(709.93, 155.4) * mm});
            skLineSegment(sketch, "E717.bottom", {"start": v(733.43, 135.09) * mm, "end": v(-733.43, 135.09) * mm});
            skLineSegment(sketch, "E717.top", {"start": v(733.43, 131.91) * mm, "end": v(-733.43, 131.91) * mm});
            skLineSegment(sketch, "E717.left", {"start": v(733.43, 135.09) * mm, "end": v(733.43, 131.91) * mm});
            skLineSegment(sketch, "E717.right", {"start": v(-733.43, 135.09) * mm, "end": v(-733.43, 131.91) * mm});
            skLineSegment(sketch, "E718.bottom", {"start": v(-733.43, -135.09) * mm, "end": v(733.43, -135.09) * mm});
            skLineSegment(sketch, "E718.top", {"start": v(-733.43, -131.91) * mm, "end": v(733.43, -131.91) * mm});
            skLineSegment(sketch, "E718.left", {"start": v(-733.43, -135.09) * mm, "end": v(-733.43, -131.91) * mm});
            skLineSegment(sketch, "E718.right", {"start": v(733.43, -135.09) * mm, "end": v(733.43, -131.91) * mm});
            skSolve(sketch);
        }
        {
            var Q0;
            Q0 = qSketchRegion(id + "F6", true);
            extrude(context, id + "F7", {"entities" : qUnion([Q0]), "oppositeDirection" : true, "depth" : 3.05 * mm, "offsetDistance" : 25.4 * mm});
        }
    });
